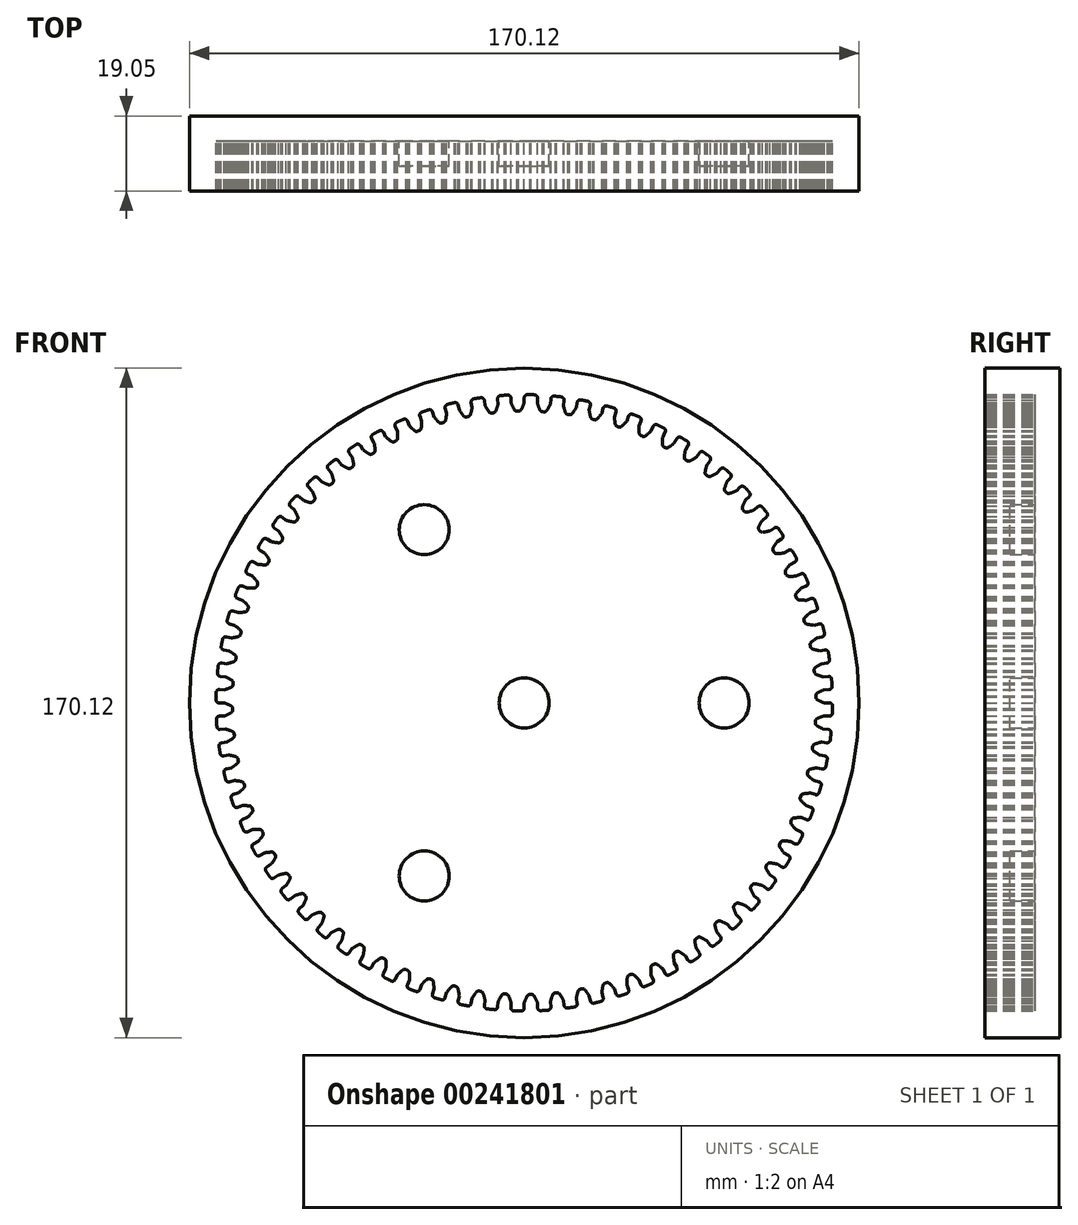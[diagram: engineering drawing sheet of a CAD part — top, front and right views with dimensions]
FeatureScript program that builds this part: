
annotation { "Feature Type Name" : "Feature", "Feature Type Description" : "" }
export const myFeature = defineFeature(function(context is Context, id is Id, definition is map)
    precondition{}
    {
        {
            var Q0;
            Q0=qCreatedBy(makeId("Front.planeOp"),FACE);
            var sketch = newSketch(context, id + "F0", { "sketchPlane" : qUnion([Q0])});
            skArc(sketch, "E0", {"start": v(-4.21, 78.2) * mm, "mid": v(-5.12, 78.15) * mm, "end": v(-6.03, 78.08) * mm});
            skLineSegment(sketch, "E1.MirrorCS", {"start": v(0, 76.2) * mm, "end": v(0, 77.53) * mm});
            skArc(sketch, "E2.MirrorCS", {"start": v(0, 76.2) * mm, "mid": v(-0.35, 75.36) * mm, "end": v(-0.73, 74.54) * mm});
            skArc(sketch, "E3.MirrorCS", {"start": v(-3.32, 76.13) * mm, "mid": v(-2.94, 75.3) * mm, "end": v(-2.52, 74.5) * mm});
            skLineSegment(sketch, "E4.MirrorCS", {"start": v(-3.32, 76.13) * mm, "end": v(-3.38, 77.45) * mm});
            skPoint(sketch, "E5.visualSharp", {"position": v(-2.27, 74.06) * mm});
            skArc(sketch, "E5.filletArc", {"start": v(-2.52, 74.5) * mm, "mid": v(-2.2, 74.19) * mm, "end": v(-1.78, 74.1) * mm});
            skPoint(sketch, "E6.visualSharp", {"position": v(-0.96, 74.09) * mm});
            skArc(sketch, "E6.filletArc", {"start": v(-1.45, 74.1) * mm, "mid": v(-1.03, 74.21) * mm, "end": v(-0.73, 74.54) * mm});
            skLineSegment(sketch, "E7", {"start": v(-1.78, 74.1) * mm, "end": v(-1.45, 74.1) * mm});
            skCircle(sketch, "E8", {"center": v(0, 0) * mm, "radius": 85.06 * mm});
            skPoint(sketch, "E9.visualSharp", {"position": v(-3.42, 78.24) * mm});
            skPoint(sketch, "E10.visualSharp", {"position": v(0, 78.32) * mm});
            skArc(sketch, "E11.filletArc", {"start": v(0.8, 78.31) * mm, "mid": v(0.23, 78.08) * mm, "end": v(0, 77.53) * mm});
            skArc(sketch, "E12.filletArc", {"start": v(-3.38, 77.45) * mm, "mid": v(-3.64, 78) * mm, "end": v(-4.21, 78.2) * mm});
            skArc(sketch, "E13.1.0", {"start": v(-10.12, 76.86) * mm, "mid": v(-10.42, 77.39) * mm, "end": v(-11.01, 77.54) * mm});
            skLineSegment(sketch, "E13.1.1", {"start": v(-9.95, 75.55) * mm, "end": v(-10.12, 76.86) * mm});
            skArc(sketch, "E13.1.2", {"start": v(-9.95, 75.55) * mm, "mid": v(-9.5, 74.76) * mm, "end": v(-9, 74) * mm});
            skArc(sketch, "E13.1.3", {"start": v(-9, 74) * mm, "mid": v(-8.66, 73.71) * mm, "end": v(-8.23, 73.66) * mm});
            skLineSegment(sketch, "E13.1.4", {"start": v(-8.23, 73.66) * mm, "end": v(-7.9, 73.7) * mm});
            skArc(sketch, "E13.1.5", {"start": v(-7.9, 73.7) * mm, "mid": v(-7.5, 73.84) * mm, "end": v(-7.23, 74.19) * mm});
            skArc(sketch, "E13.1.6", {"start": v(-6.64, 75.91) * mm, "mid": v(-6.91, 75.04) * mm, "end": v(-7.23, 74.19) * mm});
            skLineSegment(sketch, "E13.1.7", {"start": v(-6.64, 75.91) * mm, "end": v(-6.76, 77.23) * mm});
            skArc(sketch, "E13.1.8", {"start": v(-6.03, 78.08) * mm, "mid": v(-6.57, 77.8) * mm, "end": v(-6.76, 77.23) * mm});
            skArc(sketch, "E13.2.0", {"start": v(-16.78, 75.69) * mm, "mid": v(-17.13, 76.18) * mm, "end": v(-17.73, 76.28) * mm});
            skLineSegment(sketch, "E13.2.1", {"start": v(-16.5, 74.4) * mm, "end": v(-16.78, 75.69) * mm});
            skArc(sketch, "E13.2.2", {"start": v(-16.5, 74.4) * mm, "mid": v(-15.97, 73.65) * mm, "end": v(-15.42, 72.93) * mm});
            skArc(sketch, "E13.2.3", {"start": v(-15.42, 72.93) * mm, "mid": v(-15.06, 72.68) * mm, "end": v(-14.62, 72.66) * mm});
            skLineSegment(sketch, "E13.2.4", {"start": v(-14.62, 72.66) * mm, "end": v(-14.3, 72.72) * mm});
            skArc(sketch, "E13.2.5", {"start": v(-14.3, 72.72) * mm, "mid": v(-13.9, 72.9) * mm, "end": v(-13.66, 73.28) * mm});
            skArc(sketch, "E13.2.6", {"start": v(-13.23, 75.04) * mm, "mid": v(-13.43, 74.15) * mm, "end": v(-13.66, 73.28) * mm});
            skLineSegment(sketch, "E13.2.7", {"start": v(-13.23, 75.04) * mm, "end": v(-13.46, 76.35) * mm});
            skArc(sketch, "E13.2.8", {"start": v(-12.82, 77.26) * mm, "mid": v(-13.33, 76.94) * mm, "end": v(-13.46, 76.35) * mm});
            skArc(sketch, "E14.1.3.0", {"start": v(-23.31, 73.94) * mm, "mid": v(-23.7, 74.4) * mm, "end": v(-24.3, 74.45) * mm});
            skLineSegment(sketch, "E14.4.3.0", {"start": v(-22.91, 72.67) * mm, "end": v(-23.31, 73.94) * mm});
            skArc(sketch, "E14.7.3.0", {"start": v(-22.91, 72.67) * mm, "mid": v(-22.33, 71.98) * mm, "end": v(-21.71, 71.3) * mm});
            skArc(sketch, "E14.11.3.0", {"start": v(-21.71, 71.3) * mm, "mid": v(-21.33, 71.09) * mm, "end": v(-20.9, 71.1) * mm});
            skLineSegment(sketch, "E14.15.3.0", {"start": v(-20.9, 71.1) * mm, "end": v(-20.58, 71.2) * mm});
            skArc(sketch, "E14.18.3.0", {"start": v(-20.58, 71.2) * mm, "mid": v(-20.2, 71.42) * mm, "end": v(-20, 71.8) * mm});
            skArc(sketch, "E14.22.3.0", {"start": v(-19.72, 73.6) * mm, "mid": v(-19.84, 72.7) * mm, "end": v(-20, 71.8) * mm});
            skLineSegment(sketch, "E14.26.3.0", {"start": v(-19.72, 73.6) * mm, "end": v(-20.07, 74.88) * mm});
            skArc(sketch, "E14.29.3.0", {"start": v(-19.5, 75.85) * mm, "mid": v(-19.98, 75.48) * mm, "end": v(-20.07, 74.88) * mm});
            skArc(sketch, "E14.1.4.0", {"start": v(-29.67, 71.62) * mm, "mid": v(-30.1, 72.05) * mm, "end": v(-30.7, 72.05) * mm});
            skLineSegment(sketch, "E14.4.4.0", {"start": v(-29.16, 70.4) * mm, "end": v(-29.67, 71.62) * mm});
            skArc(sketch, "E14.7.4.0", {"start": v(-29.16, 70.4) * mm, "mid": v(-28.52, 69.76) * mm, "end": v(-27.85, 69.14) * mm});
            skArc(sketch, "E14.11.4.0", {"start": v(-27.85, 69.14) * mm, "mid": v(-27.45, 68.96) * mm, "end": v(-27.01, 69.02) * mm});
            skLineSegment(sketch, "E14.15.4.0", {"start": v(-27.01, 69.02) * mm, "end": v(-26.71, 69.13) * mm});
            skArc(sketch, "E14.18.4.0", {"start": v(-26.71, 69.13) * mm, "mid": v(-26.35, 69.39) * mm, "end": v(-26.18, 69.79) * mm});
            skArc(sketch, "E14.22.4.0", {"start": v(-26.06, 71.6) * mm, "mid": v(-26.1, 70.7) * mm, "end": v(-26.18, 69.79) * mm});
            skLineSegment(sketch, "E14.26.4.0", {"start": v(-26.06, 71.6) * mm, "end": v(-26.52, 72.85) * mm});
            skArc(sketch, "E14.29.4.0", {"start": v(-26.04, 73.86) * mm, "mid": v(-26.49, 73.46) * mm, "end": v(-26.52, 72.85) * mm});
            skArc(sketch, "E14.1.5.0", {"start": v(-35.8, 68.77) * mm, "mid": v(-36.26, 69.15) * mm, "end": v(-36.87, 69.1) * mm});
            skLineSegment(sketch, "E14.4.5.0", {"start": v(-35.19, 67.6) * mm, "end": v(-35.8, 68.77) * mm});
            skArc(sketch, "E14.7.5.0", {"start": v(-35.19, 67.6) * mm, "mid": v(-34.49, 67) * mm, "end": v(-33.77, 66.45) * mm});
            skArc(sketch, "E14.11.5.0", {"start": v(-33.77, 66.45) * mm, "mid": v(-33.35, 66.3) * mm, "end": v(-32.93, 66.4) * mm});
            skLineSegment(sketch, "E14.15.5.0", {"start": v(-32.93, 66.4) * mm, "end": v(-32.63, 66.54) * mm});
            skArc(sketch, "E14.18.5.0", {"start": v(-32.63, 66.54) * mm, "mid": v(-32.3, 66.82) * mm, "end": v(-32.16, 67.24) * mm});
            skArc(sketch, "E14.22.5.0", {"start": v(-32.2, 69.06) * mm, "mid": v(-32.16, 68.15) * mm, "end": v(-32.16, 67.24) * mm});
            skLineSegment(sketch, "E14.26.5.0", {"start": v(-32.2, 69.06) * mm, "end": v(-32.76, 70.26) * mm});
            skArc(sketch, "E14.29.5.0", {"start": v(-32.38, 71.31) * mm, "mid": v(-32.79, 70.87) * mm, "end": v(-32.76, 70.26) * mm});
            skArc(sketch, "E14.1.6.0", {"start": v(-41.65, 65.38) * mm, "mid": v(-42.15, 65.73) * mm, "end": v(-42.75, 65.62) * mm});
            skLineSegment(sketch, "E14.4.6.0", {"start": v(-40.94, 64.27) * mm, "end": v(-41.65, 65.38) * mm});
            skArc(sketch, "E14.7.6.0", {"start": v(-40.94, 64.27) * mm, "mid": v(-40.2, 63.74) * mm, "end": v(-39.43, 63.26) * mm});
            skArc(sketch, "E14.11.6.0", {"start": v(-39.43, 63.26) * mm, "mid": v(-39, 63.14) * mm, "end": v(-38.59, 63.28) * mm});
            skLineSegment(sketch, "E14.15.6.0", {"start": v(-38.59, 63.28) * mm, "end": v(-38.3, 63.45) * mm});
            skArc(sketch, "E14.18.6.0", {"start": v(-38.3, 63.45) * mm, "mid": v(-38, 63.76) * mm, "end": v(-37.9, 64.18) * mm});
            skArc(sketch, "E14.22.6.0", {"start": v(-38.1, 66) * mm, "mid": v(-37.98, 65.09) * mm, "end": v(-37.9, 64.18) * mm});
            skLineSegment(sketch, "E14.26.6.0", {"start": v(-38.1, 66) * mm, "end": v(-38.76, 67.14) * mm});
            skArc(sketch, "E14.29.6.0", {"start": v(-38.47, 68.22) * mm, "mid": v(-38.84, 67.74) * mm, "end": v(-38.76, 67.14) * mm});
            skArc(sketch, "E14.1.7.0", {"start": v(-47.2, 61.5) * mm, "mid": v(-47.72, 61.8) * mm, "end": v(-48.3, 61.65) * mm});
            skLineSegment(sketch, "E14.4.7.0", {"start": v(-46.39, 60.45) * mm, "end": v(-47.2, 61.5) * mm});
            skArc(sketch, "E14.7.7.0", {"start": v(-46.39, 60.45) * mm, "mid": v(-45.6, 60) * mm, "end": v(-44.8, 59.58) * mm});
            skArc(sketch, "E14.11.7.0", {"start": v(-44.8, 59.58) * mm, "mid": v(-44.36, 59.5) * mm, "end": v(-43.96, 59.67) * mm});
            skLineSegment(sketch, "E14.15.7.0", {"start": v(-43.96, 59.67) * mm, "end": v(-43.7, 59.86) * mm});
            skArc(sketch, "E14.18.7.0", {"start": v(-43.7, 59.86) * mm, "mid": v(-43.41, 60.2) * mm, "end": v(-43.35, 60.64) * mm});
            skArc(sketch, "E14.22.7.0", {"start": v(-43.7, 62.42) * mm, "mid": v(-43.5, 61.53) * mm, "end": v(-43.35, 60.64) * mm});
            skLineSegment(sketch, "E14.26.7.0", {"start": v(-43.7, 62.42) * mm, "end": v(-44.47, 63.5) * mm});
            skArc(sketch, "E14.29.7.0", {"start": v(-44.27, 64.6) * mm, "mid": v(-44.6, 64.1) * mm, "end": v(-44.47, 63.5) * mm});
            skArc(sketch, "E14.1.8.0", {"start": v(-52.38, 57.16) * mm, "mid": v(-52.93, 57.41) * mm, "end": v(-53.5, 57.2) * mm});
            skLineSegment(sketch, "E14.4.8.0", {"start": v(-51.48, 56.18) * mm, "end": v(-52.38, 57.16) * mm});
            skArc(sketch, "E14.7.8.0", {"start": v(-51.48, 56.18) * mm, "mid": v(-50.66, 55.8) * mm, "end": v(-49.82, 55.45) * mm});
            skArc(sketch, "E14.11.8.0", {"start": v(-49.82, 55.45) * mm, "mid": v(-49.38, 55.41) * mm, "end": v(-48.99, 55.62) * mm});
            skLineSegment(sketch, "E14.15.8.0", {"start": v(-48.99, 55.62) * mm, "end": v(-48.75, 55.83) * mm});
            skArc(sketch, "E14.18.8.0", {"start": v(-48.75, 55.83) * mm, "mid": v(-48.5, 56.19) * mm, "end": v(-48.47, 56.63) * mm});
            skArc(sketch, "E14.22.8.0", {"start": v(-48.98, 58.37) * mm, "mid": v(-48.7, 57.5) * mm, "end": v(-48.47, 56.63) * mm});
            skLineSegment(sketch, "E14.26.8.0", {"start": v(-48.98, 58.37) * mm, "end": v(-49.83, 59.39) * mm});
            skArc(sketch, "E14.29.8.0", {"start": v(-49.73, 60.5) * mm, "mid": v(-50.01, 59.97) * mm, "end": v(-49.83, 59.39) * mm});
            skArc(sketch, "E14.1.9.0", {"start": v(-57.16, 52.38) * mm, "mid": v(-57.73, 52.58) * mm, "end": v(-58.28, 52.32) * mm});
            skLineSegment(sketch, "E14.4.9.0", {"start": v(-56.18, 51.48) * mm, "end": v(-57.16, 52.38) * mm});
            skArc(sketch, "E14.7.9.0", {"start": v(-56.18, 51.48) * mm, "mid": v(-55.33, 51.17) * mm, "end": v(-54.46, 50.9) * mm});
            skArc(sketch, "E14.11.9.0", {"start": v(-54.46, 50.9) * mm, "mid": v(-54.02, 50.9) * mm, "end": v(-53.65, 51.13) * mm});
            skLineSegment(sketch, "E14.15.9.0", {"start": v(-53.65, 51.13) * mm, "end": v(-53.43, 51.37) * mm});
            skArc(sketch, "E14.18.9.0", {"start": v(-53.43, 51.37) * mm, "mid": v(-53.2, 51.75) * mm, "end": v(-53.22, 52.19) * mm});
            skArc(sketch, "E14.22.9.0", {"start": v(-53.88, 53.88) * mm, "mid": v(-53.53, 53.04) * mm, "end": v(-53.22, 52.19) * mm});
            skLineSegment(sketch, "E14.26.9.0", {"start": v(-53.88, 53.88) * mm, "end": v(-54.82, 54.82) * mm});
            skArc(sketch, "E14.29.9.0", {"start": v(-54.81, 55.94) * mm, "mid": v(-55.05, 55.38) * mm, "end": v(-54.82, 54.82) * mm});
            skArc(sketch, "E14.1.10.0", {"start": v(-61.5, 47.2) * mm, "mid": v(-62.1, 47.35) * mm, "end": v(-62.61, 47.04) * mm});
            skLineSegment(sketch, "E14.4.10.0", {"start": v(-60.45, 46.39) * mm, "end": v(-61.5, 47.2) * mm});
            skArc(sketch, "E14.7.10.0", {"start": v(-60.45, 46.39) * mm, "mid": v(-59.58, 46.15) * mm, "end": v(-58.69, 45.96) * mm});
            skArc(sketch, "E14.11.10.0", {"start": v(-58.69, 45.96) * mm, "mid": v(-58.25, 46) * mm, "end": v(-57.9, 46.26) * mm});
            skLineSegment(sketch, "E14.15.10.0", {"start": v(-57.9, 46.26) * mm, "end": v(-57.7, 46.52) * mm});
            skArc(sketch, "E14.18.10.0", {"start": v(-57.7, 46.52) * mm, "mid": v(-57.51, 46.91) * mm, "end": v(-57.57, 47.35) * mm});
            skArc(sketch, "E14.22.10.0", {"start": v(-58.37, 48.98) * mm, "mid": v(-57.95, 48.17) * mm, "end": v(-57.57, 47.35) * mm});
            skLineSegment(sketch, "E14.26.10.0", {"start": v(-58.37, 48.98) * mm, "end": v(-59.39, 49.83) * mm});
            skArc(sketch, "E14.29.10.0", {"start": v(-59.48, 50.95) * mm, "mid": v(-59.67, 50.37) * mm, "end": v(-59.39, 49.83) * mm});
            skArc(sketch, "E14.1.11.0", {"start": v(-65.38, 41.65) * mm, "mid": v(-65.98, 41.76) * mm, "end": v(-66.48, 41.4) * mm});
            skLineSegment(sketch, "E14.4.11.0", {"start": v(-64.27, 40.94) * mm, "end": v(-65.38, 41.65) * mm});
            skArc(sketch, "E14.7.11.0", {"start": v(-64.27, 40.94) * mm, "mid": v(-63.37, 40.78) * mm, "end": v(-62.47, 40.67) * mm});
            skArc(sketch, "E14.11.11.0", {"start": v(-62.47, 40.67) * mm, "mid": v(-62.04, 40.74) * mm, "end": v(-61.71, 41.04) * mm});
            skLineSegment(sketch, "E14.15.11.0", {"start": v(-61.71, 41.04) * mm, "end": v(-61.53, 41.31) * mm});
            skArc(sketch, "E14.18.11.0", {"start": v(-61.53, 41.31) * mm, "mid": v(-61.38, 41.72) * mm, "end": v(-61.48, 42.15) * mm});
            skArc(sketch, "E14.22.11.0", {"start": v(-62.42, 43.7) * mm, "mid": v(-61.93, 42.94) * mm, "end": v(-61.48, 42.15) * mm});
            skLineSegment(sketch, "E14.26.11.0", {"start": v(-62.42, 43.7) * mm, "end": v(-63.5, 44.47) * mm});
            skArc(sketch, "E14.29.11.0", {"start": v(-63.7, 45.57) * mm, "mid": v(-63.83, 44.98) * mm, "end": v(-63.5, 44.47) * mm});
            skArc(sketch, "E14.1.12.0", {"start": v(-68.77, 35.8) * mm, "mid": v(-69.37, 35.85) * mm, "end": v(-69.83, 35.46) * mm});
            skLineSegment(sketch, "E14.4.12.0", {"start": v(-67.6, 35.19) * mm, "end": v(-68.77, 35.8) * mm});
            skArc(sketch, "E14.7.12.0", {"start": v(-67.6, 35.19) * mm, "mid": v(-66.68, 35.1) * mm, "end": v(-65.78, 35.07) * mm});
            skArc(sketch, "E14.11.12.0", {"start": v(-65.78, 35.07) * mm, "mid": v(-65.35, 35.18) * mm, "end": v(-65.06, 35.5) * mm});
            skLineSegment(sketch, "E14.15.12.0", {"start": v(-65.06, 35.5) * mm, "end": v(-64.9, 35.8) * mm});
            skArc(sketch, "E14.18.12.0", {"start": v(-64.9, 35.8) * mm, "mid": v(-64.79, 36.21) * mm, "end": v(-64.92, 36.63) * mm});
            skArc(sketch, "E14.22.12.0", {"start": v(-66, 38.1) * mm, "mid": v(-65.44, 37.38) * mm, "end": v(-64.92, 36.63) * mm});
            skLineSegment(sketch, "E14.26.12.0", {"start": v(-66, 38.1) * mm, "end": v(-67.14, 38.76) * mm});
            skArc(sketch, "E14.29.12.0", {"start": v(-67.42, 39.85) * mm, "mid": v(-67.5, 39.24) * mm, "end": v(-67.14, 38.76) * mm});
            skArc(sketch, "E14.1.13.0", {"start": v(-71.62, 29.67) * mm, "mid": v(-72.23, 29.67) * mm, "end": v(-72.66, 29.23) * mm});
            skLineSegment(sketch, "E14.4.13.0", {"start": v(-70.4, 29.16) * mm, "end": v(-71.62, 29.67) * mm});
            skArc(sketch, "E14.7.13.0", {"start": v(-70.4, 29.16) * mm, "mid": v(-69.5, 29.16) * mm, "end": v(-68.58, 29.2) * mm});
            skArc(sketch, "E14.11.13.0", {"start": v(-68.58, 29.2) * mm, "mid": v(-68.17, 29.35) * mm, "end": v(-67.9, 29.7) * mm});
            skLineSegment(sketch, "E14.15.13.0", {"start": v(-67.9, 29.7) * mm, "end": v(-67.77, 30) * mm});
            skArc(sketch, "E14.18.13.0", {"start": v(-67.77, 30) * mm, "mid": v(-67.7, 30.43) * mm, "end": v(-67.86, 30.84) * mm});
            skArc(sketch, "E14.22.13.0", {"start": v(-69.06, 32.2) * mm, "mid": v(-68.45, 31.53) * mm, "end": v(-67.86, 30.84) * mm});
            skLineSegment(sketch, "E14.26.13.0", {"start": v(-69.06, 32.2) * mm, "end": v(-70.26, 32.76) * mm});
            skArc(sketch, "E14.29.13.0", {"start": v(-70.64, 33.82) * mm, "mid": v(-70.67, 33.21) * mm, "end": v(-70.26, 32.76) * mm});
            skArc(sketch, "E14.1.14.0", {"start": v(-73.94, 23.31) * mm, "mid": v(-74.54, 23.26) * mm, "end": v(-74.93, 22.8) * mm});
            skLineSegment(sketch, "E14.4.14.0", {"start": v(-72.67, 22.91) * mm, "end": v(-73.94, 23.31) * mm});
            skArc(sketch, "E14.7.14.0", {"start": v(-72.67, 22.91) * mm, "mid": v(-71.77, 23) * mm, "end": v(-70.87, 23.11) * mm});
            skArc(sketch, "E14.11.14.0", {"start": v(-70.87, 23.11) * mm, "mid": v(-70.47, 23.3) * mm, "end": v(-70.23, 23.67) * mm});
            skLineSegment(sketch, "E14.15.14.0", {"start": v(-70.23, 23.67) * mm, "end": v(-70.13, 23.98) * mm});
            skArc(sketch, "E14.18.14.0", {"start": v(-70.13, 23.98) * mm, "mid": v(-70.1, 24.41) * mm, "end": v(-70.3, 24.8) * mm});
            skArc(sketch, "E14.22.14.0", {"start": v(-71.6, 26.06) * mm, "mid": v(-70.93, 25.45) * mm, "end": v(-70.3, 24.8) * mm});
            skLineSegment(sketch, "E14.26.14.0", {"start": v(-71.6, 26.06) * mm, "end": v(-72.85, 26.52) * mm});
            skArc(sketch, "E14.29.14.0", {"start": v(-73.32, 27.53) * mm, "mid": v(-73.3, 26.93) * mm, "end": v(-72.85, 26.52) * mm});
            skArc(sketch, "E14.1.15.0", {"start": v(-75.69, 16.78) * mm, "mid": v(-76.28, 16.67) * mm, "end": v(-76.63, 16.17) * mm});
            skLineSegment(sketch, "E14.4.15.0", {"start": v(-74.4, 16.5) * mm, "end": v(-75.69, 16.78) * mm});
            skArc(sketch, "E14.7.15.0", {"start": v(-74.4, 16.5) * mm, "mid": v(-73.5, 16.65) * mm, "end": v(-72.61, 16.85) * mm});
            skArc(sketch, "E14.11.15.0", {"start": v(-72.61, 16.85) * mm, "mid": v(-72.23, 17.07) * mm, "end": v(-72.03, 17.46) * mm});
            skLineSegment(sketch, "E14.15.15.0", {"start": v(-72.03, 17.46) * mm, "end": v(-71.95, 17.77) * mm});
            skArc(sketch, "E14.18.15.0", {"start": v(-71.95, 17.77) * mm, "mid": v(-71.95, 18.21) * mm, "end": v(-72.19, 18.58) * mm});
            skArc(sketch, "E14.22.15.0", {"start": v(-73.6, 19.72) * mm, "mid": v(-72.88, 19.17) * mm, "end": v(-72.19, 18.58) * mm});
            skLineSegment(sketch, "E14.26.15.0", {"start": v(-73.6, 19.72) * mm, "end": v(-74.88, 20.07) * mm});
            skArc(sketch, "E14.29.15.0", {"start": v(-75.44, 21.04) * mm, "mid": v(-75.36, 20.44) * mm, "end": v(-74.88, 20.07) * mm});
            skArc(sketch, "E14.1.16.0", {"start": v(-76.86, 10.12) * mm, "mid": v(-77.45, 9.96) * mm, "end": v(-77.75, 9.43) * mm});
            skLineSegment(sketch, "E14.4.16.0", {"start": v(-75.55, 9.95) * mm, "end": v(-76.86, 10.12) * mm});
            skArc(sketch, "E14.7.16.0", {"start": v(-75.55, 9.95) * mm, "mid": v(-74.67, 10.18) * mm, "end": v(-73.8, 10.46) * mm});
            skArc(sketch, "E14.11.16.0", {"start": v(-73.8, 10.46) * mm, "mid": v(-73.44, 10.7) * mm, "end": v(-73.28, 11.11) * mm});
            skLineSegment(sketch, "E14.15.16.0", {"start": v(-73.28, 11.11) * mm, "end": v(-73.23, 11.43) * mm});
            skArc(sketch, "E14.18.16.0", {"start": v(-73.23, 11.43) * mm, "mid": v(-73.26, 11.87) * mm, "end": v(-73.53, 12.22) * mm});
            skArc(sketch, "E14.22.16.0", {"start": v(-75.04, 13.23) * mm, "mid": v(-74.27, 12.74) * mm, "end": v(-73.53, 12.22) * mm});
            skLineSegment(sketch, "E14.26.16.0", {"start": v(-75.04, 13.23) * mm, "end": v(-76.35, 13.46) * mm});
            skArc(sketch, "E14.29.16.0", {"start": v(-76.98, 14.38) * mm, "mid": v(-76.86, 13.79) * mm, "end": v(-76.35, 13.46) * mm});
            skArc(sketch, "E14.1.17.0", {"start": v(-77.45, 3.38) * mm, "mid": v(-78.02, 3.17) * mm, "end": v(-78.27, 2.62) * mm});
            skLineSegment(sketch, "E14.4.17.0", {"start": v(-76.13, 3.32) * mm, "end": v(-77.45, 3.38) * mm});
            skArc(sketch, "E14.7.17.0", {"start": v(-76.13, 3.32) * mm, "mid": v(-75.27, 3.63) * mm, "end": v(-74.43, 3.98) * mm});
            skArc(sketch, "E14.11.17.0", {"start": v(-74.43, 3.98) * mm, "mid": v(-74.1, 4.27) * mm, "end": v(-73.97, 4.69) * mm});
            skLineSegment(sketch, "E14.15.17.0", {"start": v(-73.97, 4.69) * mm, "end": v(-73.94, 5) * mm});
            skArc(sketch, "E14.18.17.0", {"start": v(-73.94, 5) * mm, "mid": v(-74.02, 5.44) * mm, "end": v(-74.32, 5.77) * mm});
            skArc(sketch, "E14.22.17.0", {"start": v(-75.91, 6.64) * mm, "mid": v(-75.1, 6.22) * mm, "end": v(-74.32, 5.77) * mm});
            skLineSegment(sketch, "E14.26.17.0", {"start": v(-75.91, 6.64) * mm, "end": v(-77.23, 6.76) * mm});
            skArc(sketch, "E14.29.17.0", {"start": v(-77.95, 7.62) * mm, "mid": v(-77.77, 7.04) * mm, "end": v(-77.23, 6.76) * mm});
            skArc(sketch, "E14.1.18.0", {"start": v(-77.45, -3.38) * mm, "mid": v(-78, -3.64) * mm, "end": v(-78.2, -4.21) * mm});
            skLineSegment(sketch, "E14.4.18.0", {"start": v(-76.13, -3.32) * mm, "end": v(-77.45, -3.38) * mm});
            skArc(sketch, "E14.7.18.0", {"start": v(-76.13, -3.32) * mm, "mid": v(-75.3, -2.94) * mm, "end": v(-74.5, -2.52) * mm});
            skArc(sketch, "E14.11.18.0", {"start": v(-74.5, -2.52) * mm, "mid": v(-74.19, -2.2) * mm, "end": v(-74.1, -1.78) * mm});
            skLineSegment(sketch, "E14.15.18.0", {"start": v(-74.1, -1.78) * mm, "end": v(-74.1, -1.45) * mm});
            skArc(sketch, "E14.18.18.0", {"start": v(-74.1, -1.45) * mm, "mid": v(-74.21, -1.03) * mm, "end": v(-74.54, -0.73) * mm});
            skArc(sketch, "E14.22.18.0", {"start": v(-76.2, 0) * mm, "mid": v(-75.36, -0.35) * mm, "end": v(-74.54, -0.73) * mm});
            skLineSegment(sketch, "E14.26.18.0", {"start": v(-76.2, 0) * mm, "end": v(-77.53, 0) * mm});
            skArc(sketch, "E14.29.18.0", {"start": v(-78.31, 0.8) * mm, "mid": v(-78.08, 0.23) * mm, "end": v(-77.53, 0) * mm});
            skArc(sketch, "E14.1.19.0", {"start": v(-76.86, -10.12) * mm, "mid": v(-77.39, -10.42) * mm, "end": v(-77.54, -11.01) * mm});
            skLineSegment(sketch, "E14.4.19.0", {"start": v(-75.55, -9.95) * mm, "end": v(-76.86, -10.12) * mm});
            skArc(sketch, "E14.7.19.0", {"start": v(-75.55, -9.95) * mm, "mid": v(-74.76, -9.5) * mm, "end": v(-74, -9) * mm});
            skArc(sketch, "E14.11.19.0", {"start": v(-74, -9) * mm, "mid": v(-73.71, -8.66) * mm, "end": v(-73.66, -8.23) * mm});
            skLineSegment(sketch, "E14.15.19.0", {"start": v(-73.66, -8.23) * mm, "end": v(-73.7, -7.9) * mm});
            skArc(sketch, "E14.18.19.0", {"start": v(-73.7, -7.9) * mm, "mid": v(-73.84, -7.5) * mm, "end": v(-74.19, -7.23) * mm});
            skArc(sketch, "E14.22.19.0", {"start": v(-75.91, -6.64) * mm, "mid": v(-75.04, -6.91) * mm, "end": v(-74.19, -7.23) * mm});
            skLineSegment(sketch, "E14.26.19.0", {"start": v(-75.91, -6.64) * mm, "end": v(-77.23, -6.76) * mm});
            skArc(sketch, "E14.29.19.0", {"start": v(-78.08, -6.03) * mm, "mid": v(-77.8, -6.57) * mm, "end": v(-77.23, -6.76) * mm});
            skArc(sketch, "E14.1.20.0", {"start": v(-75.69, -16.78) * mm, "mid": v(-76.18, -17.13) * mm, "end": v(-76.28, -17.73) * mm});
            skLineSegment(sketch, "E14.4.20.0", {"start": v(-74.4, -16.5) * mm, "end": v(-75.69, -16.78) * mm});
            skArc(sketch, "E14.7.20.0", {"start": v(-74.4, -16.5) * mm, "mid": v(-73.65, -15.97) * mm, "end": v(-72.93, -15.42) * mm});
            skArc(sketch, "E14.11.20.0", {"start": v(-72.93, -15.42) * mm, "mid": v(-72.68, -15.06) * mm, "end": v(-72.66, -14.62) * mm});
            skLineSegment(sketch, "E14.15.20.0", {"start": v(-72.66, -14.62) * mm, "end": v(-72.72, -14.3) * mm});
            skArc(sketch, "E14.18.20.0", {"start": v(-72.72, -14.3) * mm, "mid": v(-72.9, -13.9) * mm, "end": v(-73.28, -13.66) * mm});
            skArc(sketch, "E14.22.20.0", {"start": v(-75.04, -13.23) * mm, "mid": v(-74.15, -13.43) * mm, "end": v(-73.28, -13.66) * mm});
            skLineSegment(sketch, "E14.26.20.0", {"start": v(-75.04, -13.23) * mm, "end": v(-76.35, -13.46) * mm});
            skArc(sketch, "E14.29.20.0", {"start": v(-77.26, -12.82) * mm, "mid": v(-76.94, -13.33) * mm, "end": v(-76.35, -13.46) * mm});
            skArc(sketch, "E14.1.21.0", {"start": v(-73.94, -23.31) * mm, "mid": v(-74.4, -23.7) * mm, "end": v(-74.45, -24.3) * mm});
            skLineSegment(sketch, "E14.4.21.0", {"start": v(-72.67, -22.91) * mm, "end": v(-73.94, -23.31) * mm});
            skArc(sketch, "E14.7.21.0", {"start": v(-72.67, -22.91) * mm, "mid": v(-71.98, -22.33) * mm, "end": v(-71.3, -21.71) * mm});
            skArc(sketch, "E14.11.21.0", {"start": v(-71.3, -21.71) * mm, "mid": v(-71.09, -21.33) * mm, "end": v(-71.1, -20.9) * mm});
            skLineSegment(sketch, "E14.15.21.0", {"start": v(-71.1, -20.9) * mm, "end": v(-71.2, -20.58) * mm});
            skArc(sketch, "E14.18.21.0", {"start": v(-71.2, -20.58) * mm, "mid": v(-71.42, -20.2) * mm, "end": v(-71.8, -20) * mm});
            skArc(sketch, "E14.22.21.0", {"start": v(-73.6, -19.72) * mm, "mid": v(-72.7, -19.84) * mm, "end": v(-71.8, -20) * mm});
            skLineSegment(sketch, "E14.26.21.0", {"start": v(-73.6, -19.72) * mm, "end": v(-74.88, -20.07) * mm});
            skArc(sketch, "E14.29.21.0", {"start": v(-75.85, -19.5) * mm, "mid": v(-75.48, -19.98) * mm, "end": v(-74.88, -20.07) * mm});
            skArc(sketch, "E14.1.22.0", {"start": v(-71.62, -29.67) * mm, "mid": v(-72.05, -30.1) * mm, "end": v(-72.05, -30.7) * mm});
            skLineSegment(sketch, "E14.4.22.0", {"start": v(-70.4, -29.16) * mm, "end": v(-71.62, -29.67) * mm});
            skArc(sketch, "E14.7.22.0", {"start": v(-70.4, -29.16) * mm, "mid": v(-69.76, -28.52) * mm, "end": v(-69.14, -27.85) * mm});
            skArc(sketch, "E14.11.22.0", {"start": v(-69.14, -27.85) * mm, "mid": v(-68.96, -27.45) * mm, "end": v(-69.02, -27.01) * mm});
            skLineSegment(sketch, "E14.15.22.0", {"start": v(-69.02, -27.01) * mm, "end": v(-69.13, -26.71) * mm});
            skArc(sketch, "E14.18.22.0", {"start": v(-69.13, -26.71) * mm, "mid": v(-69.39, -26.35) * mm, "end": v(-69.79, -26.18) * mm});
            skArc(sketch, "E14.22.22.0", {"start": v(-71.6, -26.06) * mm, "mid": v(-70.7, -26.1) * mm, "end": v(-69.79, -26.18) * mm});
            skLineSegment(sketch, "E14.26.22.0", {"start": v(-71.6, -26.06) * mm, "end": v(-72.85, -26.52) * mm});
            skArc(sketch, "E14.29.22.0", {"start": v(-73.86, -26.04) * mm, "mid": v(-73.46, -26.49) * mm, "end": v(-72.85, -26.52) * mm});
            skArc(sketch, "E14.1.23.0", {"start": v(-68.77, -35.8) * mm, "mid": v(-69.15, -36.26) * mm, "end": v(-69.1, -36.87) * mm});
            skLineSegment(sketch, "E14.4.23.0", {"start": v(-67.6, -35.19) * mm, "end": v(-68.77, -35.8) * mm});
            skArc(sketch, "E14.7.23.0", {"start": v(-67.6, -35.19) * mm, "mid": v(-67, -34.49) * mm, "end": v(-66.45, -33.77) * mm});
            skArc(sketch, "E14.11.23.0", {"start": v(-66.45, -33.77) * mm, "mid": v(-66.3, -33.35) * mm, "end": v(-66.4, -32.93) * mm});
            skLineSegment(sketch, "E14.15.23.0", {"start": v(-66.4, -32.93) * mm, "end": v(-66.54, -32.63) * mm});
            skArc(sketch, "E14.18.23.0", {"start": v(-66.54, -32.63) * mm, "mid": v(-66.82, -32.3) * mm, "end": v(-67.24, -32.16) * mm});
            skArc(sketch, "E14.22.23.0", {"start": v(-69.06, -32.2) * mm, "mid": v(-68.15, -32.16) * mm, "end": v(-67.24, -32.16) * mm});
            skLineSegment(sketch, "E14.26.23.0", {"start": v(-69.06, -32.2) * mm, "end": v(-70.26, -32.76) * mm});
            skArc(sketch, "E14.29.23.0", {"start": v(-71.31, -32.38) * mm, "mid": v(-70.87, -32.79) * mm, "end": v(-70.26, -32.76) * mm});
            skArc(sketch, "E14.1.24.0", {"start": v(-65.38, -41.65) * mm, "mid": v(-65.73, -42.15) * mm, "end": v(-65.62, -42.75) * mm});
            skLineSegment(sketch, "E14.4.24.0", {"start": v(-64.27, -40.94) * mm, "end": v(-65.38, -41.65) * mm});
            skArc(sketch, "E14.7.24.0", {"start": v(-64.27, -40.94) * mm, "mid": v(-63.74, -40.2) * mm, "end": v(-63.26, -39.43) * mm});
            skArc(sketch, "E14.11.24.0", {"start": v(-63.26, -39.43) * mm, "mid": v(-63.14, -39) * mm, "end": v(-63.28, -38.59) * mm});
            skLineSegment(sketch, "E14.15.24.0", {"start": v(-63.28, -38.59) * mm, "end": v(-63.45, -38.3) * mm});
            skArc(sketch, "E14.18.24.0", {"start": v(-63.45, -38.3) * mm, "mid": v(-63.76, -38) * mm, "end": v(-64.18, -37.9) * mm});
            skArc(sketch, "E14.22.24.0", {"start": v(-66, -38.1) * mm, "mid": v(-65.09, -37.98) * mm, "end": v(-64.18, -37.9) * mm});
            skLineSegment(sketch, "E14.26.24.0", {"start": v(-66, -38.1) * mm, "end": v(-67.14, -38.76) * mm});
            skArc(sketch, "E14.29.24.0", {"start": v(-68.22, -38.47) * mm, "mid": v(-67.74, -38.84) * mm, "end": v(-67.14, -38.76) * mm});
            skArc(sketch, "E14.1.25.0", {"start": v(-61.5, -47.2) * mm, "mid": v(-61.8, -47.72) * mm, "end": v(-61.65, -48.3) * mm});
            skLineSegment(sketch, "E14.4.25.0", {"start": v(-60.45, -46.39) * mm, "end": v(-61.5, -47.2) * mm});
            skArc(sketch, "E14.7.25.0", {"start": v(-60.45, -46.39) * mm, "mid": v(-60, -45.6) * mm, "end": v(-59.58, -44.8) * mm});
            skArc(sketch, "E14.11.25.0", {"start": v(-59.58, -44.8) * mm, "mid": v(-59.5, -44.36) * mm, "end": v(-59.67, -43.96) * mm});
            skLineSegment(sketch, "E14.15.25.0", {"start": v(-59.67, -43.96) * mm, "end": v(-59.86, -43.7) * mm});
            skArc(sketch, "E14.18.25.0", {"start": v(-59.86, -43.7) * mm, "mid": v(-60.2, -43.41) * mm, "end": v(-60.64, -43.35) * mm});
            skArc(sketch, "E14.22.25.0", {"start": v(-62.42, -43.7) * mm, "mid": v(-61.53, -43.5) * mm, "end": v(-60.64, -43.35) * mm});
            skLineSegment(sketch, "E14.26.25.0", {"start": v(-62.42, -43.7) * mm, "end": v(-63.5, -44.47) * mm});
            skArc(sketch, "E14.29.25.0", {"start": v(-64.6, -44.27) * mm, "mid": v(-64.1, -44.6) * mm, "end": v(-63.5, -44.47) * mm});
            skArc(sketch, "E14.1.26.0", {"start": v(-57.16, -52.38) * mm, "mid": v(-57.41, -52.93) * mm, "end": v(-57.2, -53.5) * mm});
            skLineSegment(sketch, "E14.4.26.0", {"start": v(-56.18, -51.48) * mm, "end": v(-57.16, -52.38) * mm});
            skArc(sketch, "E14.7.26.0", {"start": v(-56.18, -51.48) * mm, "mid": v(-55.8, -50.66) * mm, "end": v(-55.45, -49.82) * mm});
            skArc(sketch, "E14.11.26.0", {"start": v(-55.45, -49.82) * mm, "mid": v(-55.41, -49.38) * mm, "end": v(-55.62, -48.99) * mm});
            skLineSegment(sketch, "E14.15.26.0", {"start": v(-55.62, -48.99) * mm, "end": v(-55.83, -48.75) * mm});
            skArc(sketch, "E14.18.26.0", {"start": v(-55.83, -48.75) * mm, "mid": v(-56.19, -48.5) * mm, "end": v(-56.63, -48.47) * mm});
            skArc(sketch, "E14.22.26.0", {"start": v(-58.37, -48.98) * mm, "mid": v(-57.5, -48.7) * mm, "end": v(-56.63, -48.47) * mm});
            skLineSegment(sketch, "E14.26.26.0", {"start": v(-58.37, -48.98) * mm, "end": v(-59.39, -49.83) * mm});
            skArc(sketch, "E14.29.26.0", {"start": v(-60.5, -49.73) * mm, "mid": v(-59.97, -50.01) * mm, "end": v(-59.39, -49.83) * mm});
            skArc(sketch, "E14.1.27.0", {"start": v(-52.38, -57.16) * mm, "mid": v(-52.58, -57.73) * mm, "end": v(-52.32, -58.28) * mm});
            skLineSegment(sketch, "E14.4.27.0", {"start": v(-51.48, -56.18) * mm, "end": v(-52.38, -57.16) * mm});
            skArc(sketch, "E14.7.27.0", {"start": v(-51.48, -56.18) * mm, "mid": v(-51.17, -55.33) * mm, "end": v(-50.9, -54.46) * mm});
            skArc(sketch, "E14.11.27.0", {"start": v(-50.9, -54.46) * mm, "mid": v(-50.9, -54.02) * mm, "end": v(-51.13, -53.65) * mm});
            skLineSegment(sketch, "E14.15.27.0", {"start": v(-51.13, -53.65) * mm, "end": v(-51.37, -53.43) * mm});
            skArc(sketch, "E14.18.27.0", {"start": v(-51.37, -53.43) * mm, "mid": v(-51.75, -53.2) * mm, "end": v(-52.19, -53.22) * mm});
            skArc(sketch, "E14.22.27.0", {"start": v(-53.88, -53.88) * mm, "mid": v(-53.04, -53.53) * mm, "end": v(-52.19, -53.22) * mm});
            skLineSegment(sketch, "E14.26.27.0", {"start": v(-53.88, -53.88) * mm, "end": v(-54.82, -54.82) * mm});
            skArc(sketch, "E14.29.27.0", {"start": v(-55.94, -54.81) * mm, "mid": v(-55.38, -55.05) * mm, "end": v(-54.82, -54.82) * mm});
            skArc(sketch, "E14.1.28.0", {"start": v(-47.2, -61.5) * mm, "mid": v(-47.35, -62.1) * mm, "end": v(-47.04, -62.61) * mm});
            skLineSegment(sketch, "E14.4.28.0", {"start": v(-46.39, -60.45) * mm, "end": v(-47.2, -61.5) * mm});
            skArc(sketch, "E14.7.28.0", {"start": v(-46.39, -60.45) * mm, "mid": v(-46.15, -59.58) * mm, "end": v(-45.96, -58.69) * mm});
            skArc(sketch, "E14.11.28.0", {"start": v(-45.96, -58.69) * mm, "mid": v(-46, -58.25) * mm, "end": v(-46.26, -57.9) * mm});
            skLineSegment(sketch, "E14.15.28.0", {"start": v(-46.26, -57.9) * mm, "end": v(-46.52, -57.7) * mm});
            skArc(sketch, "E14.18.28.0", {"start": v(-46.52, -57.7) * mm, "mid": v(-46.91, -57.51) * mm, "end": v(-47.35, -57.57) * mm});
            skArc(sketch, "E14.22.28.0", {"start": v(-48.98, -58.37) * mm, "mid": v(-48.17, -57.95) * mm, "end": v(-47.35, -57.57) * mm});
            skLineSegment(sketch, "E14.26.28.0", {"start": v(-48.98, -58.37) * mm, "end": v(-49.83, -59.39) * mm});
            skArc(sketch, "E14.29.28.0", {"start": v(-50.95, -59.48) * mm, "mid": v(-50.37, -59.67) * mm, "end": v(-49.83, -59.39) * mm});
            skArc(sketch, "E14.1.29.0", {"start": v(-41.65, -65.38) * mm, "mid": v(-41.76, -65.98) * mm, "end": v(-41.4, -66.48) * mm});
            skLineSegment(sketch, "E14.4.29.0", {"start": v(-40.94, -64.27) * mm, "end": v(-41.65, -65.38) * mm});
            skArc(sketch, "E14.7.29.0", {"start": v(-40.94, -64.27) * mm, "mid": v(-40.78, -63.37) * mm, "end": v(-40.67, -62.47) * mm});
            skArc(sketch, "E14.11.29.0", {"start": v(-40.67, -62.47) * mm, "mid": v(-40.74, -62.04) * mm, "end": v(-41.04, -61.71) * mm});
            skLineSegment(sketch, "E14.15.29.0", {"start": v(-41.04, -61.71) * mm, "end": v(-41.31, -61.53) * mm});
            skArc(sketch, "E14.18.29.0", {"start": v(-41.31, -61.53) * mm, "mid": v(-41.72, -61.38) * mm, "end": v(-42.15, -61.48) * mm});
            skArc(sketch, "E14.22.29.0", {"start": v(-43.7, -62.42) * mm, "mid": v(-42.94, -61.93) * mm, "end": v(-42.15, -61.48) * mm});
            skLineSegment(sketch, "E14.26.29.0", {"start": v(-43.7, -62.42) * mm, "end": v(-44.47, -63.5) * mm});
            skArc(sketch, "E14.29.29.0", {"start": v(-45.57, -63.7) * mm, "mid": v(-44.98, -63.83) * mm, "end": v(-44.47, -63.5) * mm});
            skArc(sketch, "E14.1.30.0", {"start": v(-35.8, -68.77) * mm, "mid": v(-35.85, -69.37) * mm, "end": v(-35.46, -69.83) * mm});
            skLineSegment(sketch, "E14.4.30.0", {"start": v(-35.19, -67.6) * mm, "end": v(-35.8, -68.77) * mm});
            skArc(sketch, "E14.7.30.0", {"start": v(-35.19, -67.6) * mm, "mid": v(-35.1, -66.68) * mm, "end": v(-35.07, -65.78) * mm});
            skArc(sketch, "E14.11.30.0", {"start": v(-35.07, -65.78) * mm, "mid": v(-35.18, -65.35) * mm, "end": v(-35.5, -65.06) * mm});
            skLineSegment(sketch, "E14.15.30.0", {"start": v(-35.5, -65.06) * mm, "end": v(-35.8, -64.9) * mm});
            skArc(sketch, "E14.18.30.0", {"start": v(-35.8, -64.9) * mm, "mid": v(-36.21, -64.79) * mm, "end": v(-36.63, -64.92) * mm});
            skArc(sketch, "E14.22.30.0", {"start": v(-38.1, -66) * mm, "mid": v(-37.38, -65.44) * mm, "end": v(-36.63, -64.92) * mm});
            skLineSegment(sketch, "E14.26.30.0", {"start": v(-38.1, -66) * mm, "end": v(-38.76, -67.14) * mm});
            skArc(sketch, "E14.29.30.0", {"start": v(-39.85, -67.42) * mm, "mid": v(-39.24, -67.5) * mm, "end": v(-38.76, -67.14) * mm});
            skArc(sketch, "E14.1.31.0", {"start": v(-29.67, -71.62) * mm, "mid": v(-29.67, -72.23) * mm, "end": v(-29.23, -72.66) * mm});
            skLineSegment(sketch, "E14.4.31.0", {"start": v(-29.16, -70.4) * mm, "end": v(-29.67, -71.62) * mm});
            skArc(sketch, "E14.7.31.0", {"start": v(-29.16, -70.4) * mm, "mid": v(-29.16, -69.5) * mm, "end": v(-29.2, -68.58) * mm});
            skArc(sketch, "E14.11.31.0", {"start": v(-29.2, -68.58) * mm, "mid": v(-29.35, -68.17) * mm, "end": v(-29.7, -67.9) * mm});
            skLineSegment(sketch, "E14.15.31.0", {"start": v(-29.7, -67.9) * mm, "end": v(-30, -67.77) * mm});
            skArc(sketch, "E14.18.31.0", {"start": v(-30, -67.77) * mm, "mid": v(-30.43, -67.7) * mm, "end": v(-30.84, -67.86) * mm});
            skArc(sketch, "E14.22.31.0", {"start": v(-32.2, -69.06) * mm, "mid": v(-31.53, -68.45) * mm, "end": v(-30.84, -67.86) * mm});
            skLineSegment(sketch, "E14.26.31.0", {"start": v(-32.2, -69.06) * mm, "end": v(-32.76, -70.26) * mm});
            skArc(sketch, "E14.29.31.0", {"start": v(-33.82, -70.64) * mm, "mid": v(-33.21, -70.67) * mm, "end": v(-32.76, -70.26) * mm});
            skArc(sketch, "E14.1.32.0", {"start": v(-23.31, -73.94) * mm, "mid": v(-23.26, -74.54) * mm, "end": v(-22.8, -74.93) * mm});
            skLineSegment(sketch, "E14.4.32.0", {"start": v(-22.91, -72.67) * mm, "end": v(-23.31, -73.94) * mm});
            skArc(sketch, "E14.7.32.0", {"start": v(-22.91, -72.67) * mm, "mid": v(-23, -71.77) * mm, "end": v(-23.11, -70.87) * mm});
            skArc(sketch, "E14.11.32.0", {"start": v(-23.11, -70.87) * mm, "mid": v(-23.3, -70.47) * mm, "end": v(-23.67, -70.23) * mm});
            skLineSegment(sketch, "E14.15.32.0", {"start": v(-23.67, -70.23) * mm, "end": v(-23.98, -70.13) * mm});
            skArc(sketch, "E14.18.32.0", {"start": v(-23.98, -70.13) * mm, "mid": v(-24.41, -70.1) * mm, "end": v(-24.8, -70.3) * mm});
            skArc(sketch, "E14.22.32.0", {"start": v(-26.06, -71.6) * mm, "mid": v(-25.45, -70.93) * mm, "end": v(-24.8, -70.3) * mm});
            skLineSegment(sketch, "E14.26.32.0", {"start": v(-26.06, -71.6) * mm, "end": v(-26.52, -72.85) * mm});
            skArc(sketch, "E14.29.32.0", {"start": v(-27.53, -73.32) * mm, "mid": v(-26.93, -73.3) * mm, "end": v(-26.52, -72.85) * mm});
            skArc(sketch, "E14.1.33.0", {"start": v(-16.78, -75.69) * mm, "mid": v(-16.67, -76.28) * mm, "end": v(-16.17, -76.63) * mm});
            skLineSegment(sketch, "E14.4.33.0", {"start": v(-16.5, -74.4) * mm, "end": v(-16.78, -75.69) * mm});
            skArc(sketch, "E14.7.33.0", {"start": v(-16.5, -74.4) * mm, "mid": v(-16.65, -73.5) * mm, "end": v(-16.85, -72.61) * mm});
            skArc(sketch, "E14.11.33.0", {"start": v(-16.85, -72.61) * mm, "mid": v(-17.07, -72.23) * mm, "end": v(-17.46, -72.03) * mm});
            skLineSegment(sketch, "E14.15.33.0", {"start": v(-17.46, -72.03) * mm, "end": v(-17.77, -71.95) * mm});
            skArc(sketch, "E14.18.33.0", {"start": v(-17.77, -71.95) * mm, "mid": v(-18.21, -71.95) * mm, "end": v(-18.58, -72.19) * mm});
            skArc(sketch, "E14.22.33.0", {"start": v(-19.72, -73.6) * mm, "mid": v(-19.17, -72.88) * mm, "end": v(-18.58, -72.19) * mm});
            skLineSegment(sketch, "E14.26.33.0", {"start": v(-19.72, -73.6) * mm, "end": v(-20.07, -74.88) * mm});
            skArc(sketch, "E14.29.33.0", {"start": v(-21.04, -75.44) * mm, "mid": v(-20.44, -75.36) * mm, "end": v(-20.07, -74.88) * mm});
            skArc(sketch, "E14.1.34.0", {"start": v(-10.12, -76.86) * mm, "mid": v(-9.96, -77.45) * mm, "end": v(-9.43, -77.75) * mm});
            skLineSegment(sketch, "E14.4.34.0", {"start": v(-9.95, -75.55) * mm, "end": v(-10.12, -76.86) * mm});
            skArc(sketch, "E14.7.34.0", {"start": v(-9.95, -75.55) * mm, "mid": v(-10.18, -74.67) * mm, "end": v(-10.46, -73.8) * mm});
            skArc(sketch, "E14.11.34.0", {"start": v(-10.46, -73.8) * mm, "mid": v(-10.7, -73.44) * mm, "end": v(-11.11, -73.28) * mm});
            skLineSegment(sketch, "E14.15.34.0", {"start": v(-11.11, -73.28) * mm, "end": v(-11.43, -73.23) * mm});
            skArc(sketch, "E14.18.34.0", {"start": v(-11.43, -73.23) * mm, "mid": v(-11.87, -73.26) * mm, "end": v(-12.22, -73.53) * mm});
            skArc(sketch, "E14.22.34.0", {"start": v(-13.23, -75.04) * mm, "mid": v(-12.74, -74.27) * mm, "end": v(-12.22, -73.53) * mm});
            skLineSegment(sketch, "E14.26.34.0", {"start": v(-13.23, -75.04) * mm, "end": v(-13.46, -76.35) * mm});
            skArc(sketch, "E14.29.34.0", {"start": v(-14.38, -76.98) * mm, "mid": v(-13.79, -76.86) * mm, "end": v(-13.46, -76.35) * mm});
            skArc(sketch, "E14.1.35.0", {"start": v(-3.38, -77.45) * mm, "mid": v(-3.17, -78.02) * mm, "end": v(-2.62, -78.27) * mm});
            skLineSegment(sketch, "E14.4.35.0", {"start": v(-3.32, -76.13) * mm, "end": v(-3.38, -77.45) * mm});
            skArc(sketch, "E14.7.35.0", {"start": v(-3.32, -76.13) * mm, "mid": v(-3.63, -75.27) * mm, "end": v(-3.98, -74.43) * mm});
            skArc(sketch, "E14.11.35.0", {"start": v(-3.98, -74.43) * mm, "mid": v(-4.27, -74.1) * mm, "end": v(-4.69, -73.97) * mm});
            skLineSegment(sketch, "E14.15.35.0", {"start": v(-4.69, -73.97) * mm, "end": v(-5, -73.94) * mm});
            skArc(sketch, "E14.18.35.0", {"start": v(-5, -73.94) * mm, "mid": v(-5.44, -74.02) * mm, "end": v(-5.77, -74.32) * mm});
            skArc(sketch, "E14.22.35.0", {"start": v(-6.64, -75.91) * mm, "mid": v(-6.22, -75.1) * mm, "end": v(-5.77, -74.32) * mm});
            skLineSegment(sketch, "E14.26.35.0", {"start": v(-6.64, -75.91) * mm, "end": v(-6.76, -77.23) * mm});
            skArc(sketch, "E14.29.35.0", {"start": v(-7.62, -77.95) * mm, "mid": v(-7.04, -77.77) * mm, "end": v(-6.76, -77.23) * mm});
            skArc(sketch, "E14.1.36.0", {"start": v(3.38, -77.45) * mm, "mid": v(3.64, -78) * mm, "end": v(4.21, -78.2) * mm});
            skLineSegment(sketch, "E14.4.36.0", {"start": v(3.32, -76.13) * mm, "end": v(3.38, -77.45) * mm});
            skArc(sketch, "E14.7.36.0", {"start": v(3.32, -76.13) * mm, "mid": v(2.94, -75.3) * mm, "end": v(2.52, -74.5) * mm});
            skArc(sketch, "E14.11.36.0", {"start": v(2.52, -74.5) * mm, "mid": v(2.2, -74.19) * mm, "end": v(1.78, -74.1) * mm});
            skLineSegment(sketch, "E14.15.36.0", {"start": v(1.78, -74.1) * mm, "end": v(1.45, -74.1) * mm});
            skArc(sketch, "E14.18.36.0", {"start": v(1.45, -74.1) * mm, "mid": v(1.03, -74.21) * mm, "end": v(0.73, -74.54) * mm});
            skArc(sketch, "E14.22.36.0", {"start": v(0, -76.2) * mm, "mid": v(0.35, -75.36) * mm, "end": v(0.73, -74.54) * mm});
            skLineSegment(sketch, "E14.26.36.0", {"start": v(0, -76.2) * mm, "end": v(0, -77.53) * mm});
            skArc(sketch, "E14.29.36.0", {"start": v(-0.8, -78.31) * mm, "mid": v(-0.23, -78.08) * mm, "end": v(0, -77.53) * mm});
            skArc(sketch, "E14.1.37.0", {"start": v(10.12, -76.86) * mm, "mid": v(10.42, -77.39) * mm, "end": v(11.01, -77.54) * mm});
            skLineSegment(sketch, "E14.4.37.0", {"start": v(9.95, -75.55) * mm, "end": v(10.12, -76.86) * mm});
            skArc(sketch, "E14.7.37.0", {"start": v(9.95, -75.55) * mm, "mid": v(9.5, -74.76) * mm, "end": v(9, -74) * mm});
            skArc(sketch, "E14.11.37.0", {"start": v(9, -74) * mm, "mid": v(8.66, -73.71) * mm, "end": v(8.23, -73.66) * mm});
            skLineSegment(sketch, "E14.15.37.0", {"start": v(8.23, -73.66) * mm, "end": v(7.9, -73.7) * mm});
            skArc(sketch, "E14.18.37.0", {"start": v(7.9, -73.7) * mm, "mid": v(7.5, -73.84) * mm, "end": v(7.23, -74.19) * mm});
            skArc(sketch, "E14.22.37.0", {"start": v(6.64, -75.91) * mm, "mid": v(6.91, -75.04) * mm, "end": v(7.23, -74.19) * mm});
            skLineSegment(sketch, "E14.26.37.0", {"start": v(6.64, -75.91) * mm, "end": v(6.76, -77.23) * mm});
            skArc(sketch, "E14.29.37.0", {"start": v(6.03, -78.08) * mm, "mid": v(6.57, -77.8) * mm, "end": v(6.76, -77.23) * mm});
            skArc(sketch, "E14.1.38.0", {"start": v(16.78, -75.69) * mm, "mid": v(17.13, -76.18) * mm, "end": v(17.73, -76.28) * mm});
            skLineSegment(sketch, "E14.4.38.0", {"start": v(16.5, -74.4) * mm, "end": v(16.78, -75.69) * mm});
            skArc(sketch, "E14.7.38.0", {"start": v(16.5, -74.4) * mm, "mid": v(15.97, -73.65) * mm, "end": v(15.42, -72.93) * mm});
            skArc(sketch, "E14.11.38.0", {"start": v(15.42, -72.93) * mm, "mid": v(15.06, -72.68) * mm, "end": v(14.62, -72.66) * mm});
            skLineSegment(sketch, "E14.15.38.0", {"start": v(14.62, -72.66) * mm, "end": v(14.3, -72.72) * mm});
            skArc(sketch, "E14.18.38.0", {"start": v(14.3, -72.72) * mm, "mid": v(13.9, -72.9) * mm, "end": v(13.66, -73.28) * mm});
            skArc(sketch, "E14.22.38.0", {"start": v(13.23, -75.04) * mm, "mid": v(13.43, -74.15) * mm, "end": v(13.66, -73.28) * mm});
            skLineSegment(sketch, "E14.26.38.0", {"start": v(13.23, -75.04) * mm, "end": v(13.46, -76.35) * mm});
            skArc(sketch, "E14.29.38.0", {"start": v(12.82, -77.26) * mm, "mid": v(13.33, -76.94) * mm, "end": v(13.46, -76.35) * mm});
            skArc(sketch, "E14.1.39.0", {"start": v(23.31, -73.94) * mm, "mid": v(23.7, -74.4) * mm, "end": v(24.3, -74.45) * mm});
            skLineSegment(sketch, "E14.4.39.0", {"start": v(22.91, -72.67) * mm, "end": v(23.31, -73.94) * mm});
            skArc(sketch, "E14.7.39.0", {"start": v(22.91, -72.67) * mm, "mid": v(22.33, -71.98) * mm, "end": v(21.71, -71.3) * mm});
            skArc(sketch, "E14.11.39.0", {"start": v(21.71, -71.3) * mm, "mid": v(21.33, -71.09) * mm, "end": v(20.9, -71.1) * mm});
            skLineSegment(sketch, "E14.15.39.0", {"start": v(20.9, -71.1) * mm, "end": v(20.58, -71.2) * mm});
            skArc(sketch, "E14.18.39.0", {"start": v(20.58, -71.2) * mm, "mid": v(20.2, -71.42) * mm, "end": v(20, -71.8) * mm});
            skArc(sketch, "E14.22.39.0", {"start": v(19.72, -73.6) * mm, "mid": v(19.84, -72.7) * mm, "end": v(20, -71.8) * mm});
            skLineSegment(sketch, "E14.26.39.0", {"start": v(19.72, -73.6) * mm, "end": v(20.07, -74.88) * mm});
            skArc(sketch, "E14.29.39.0", {"start": v(19.5, -75.85) * mm, "mid": v(19.98, -75.48) * mm, "end": v(20.07, -74.88) * mm});
            skArc(sketch, "E14.1.40.0", {"start": v(29.67, -71.62) * mm, "mid": v(30.1, -72.05) * mm, "end": v(30.7, -72.05) * mm});
            skLineSegment(sketch, "E14.4.40.0", {"start": v(29.16, -70.4) * mm, "end": v(29.67, -71.62) * mm});
            skArc(sketch, "E14.7.40.0", {"start": v(29.16, -70.4) * mm, "mid": v(28.52, -69.76) * mm, "end": v(27.85, -69.14) * mm});
            skArc(sketch, "E14.11.40.0", {"start": v(27.85, -69.14) * mm, "mid": v(27.45, -68.96) * mm, "end": v(27.01, -69.02) * mm});
            skLineSegment(sketch, "E14.15.40.0", {"start": v(27.01, -69.02) * mm, "end": v(26.71, -69.13) * mm});
            skArc(sketch, "E14.18.40.0", {"start": v(26.71, -69.13) * mm, "mid": v(26.35, -69.39) * mm, "end": v(26.18, -69.79) * mm});
            skArc(sketch, "E14.22.40.0", {"start": v(26.06, -71.6) * mm, "mid": v(26.1, -70.7) * mm, "end": v(26.18, -69.79) * mm});
            skLineSegment(sketch, "E14.26.40.0", {"start": v(26.06, -71.6) * mm, "end": v(26.52, -72.85) * mm});
            skArc(sketch, "E14.29.40.0", {"start": v(26.04, -73.86) * mm, "mid": v(26.49, -73.46) * mm, "end": v(26.52, -72.85) * mm});
            skArc(sketch, "E14.1.41.0", {"start": v(35.8, -68.77) * mm, "mid": v(36.26, -69.15) * mm, "end": v(36.87, -69.1) * mm});
            skLineSegment(sketch, "E14.4.41.0", {"start": v(35.19, -67.6) * mm, "end": v(35.8, -68.77) * mm});
            skArc(sketch, "E14.7.41.0", {"start": v(35.19, -67.6) * mm, "mid": v(34.49, -67) * mm, "end": v(33.77, -66.45) * mm});
            skArc(sketch, "E14.11.41.0", {"start": v(33.77, -66.45) * mm, "mid": v(33.35, -66.3) * mm, "end": v(32.93, -66.4) * mm});
            skLineSegment(sketch, "E14.15.41.0", {"start": v(32.93, -66.4) * mm, "end": v(32.63, -66.54) * mm});
            skArc(sketch, "E14.18.41.0", {"start": v(32.63, -66.54) * mm, "mid": v(32.3, -66.82) * mm, "end": v(32.16, -67.24) * mm});
            skArc(sketch, "E14.22.41.0", {"start": v(32.2, -69.06) * mm, "mid": v(32.16, -68.15) * mm, "end": v(32.16, -67.24) * mm});
            skLineSegment(sketch, "E14.26.41.0", {"start": v(32.2, -69.06) * mm, "end": v(32.76, -70.26) * mm});
            skArc(sketch, "E14.29.41.0", {"start": v(32.38, -71.31) * mm, "mid": v(32.79, -70.87) * mm, "end": v(32.76, -70.26) * mm});
            skArc(sketch, "E14.1.42.0", {"start": v(41.65, -65.38) * mm, "mid": v(42.15, -65.73) * mm, "end": v(42.75, -65.62) * mm});
            skLineSegment(sketch, "E14.4.42.0", {"start": v(40.94, -64.27) * mm, "end": v(41.65, -65.38) * mm});
            skArc(sketch, "E14.7.42.0", {"start": v(40.94, -64.27) * mm, "mid": v(40.2, -63.74) * mm, "end": v(39.43, -63.26) * mm});
            skArc(sketch, "E14.11.42.0", {"start": v(39.43, -63.26) * mm, "mid": v(39, -63.14) * mm, "end": v(38.59, -63.28) * mm});
            skLineSegment(sketch, "E14.15.42.0", {"start": v(38.59, -63.28) * mm, "end": v(38.3, -63.45) * mm});
            skArc(sketch, "E14.18.42.0", {"start": v(38.3, -63.45) * mm, "mid": v(38, -63.76) * mm, "end": v(37.9, -64.18) * mm});
            skArc(sketch, "E14.22.42.0", {"start": v(38.1, -66) * mm, "mid": v(37.98, -65.09) * mm, "end": v(37.9, -64.18) * mm});
            skLineSegment(sketch, "E14.26.42.0", {"start": v(38.1, -66) * mm, "end": v(38.76, -67.14) * mm});
            skArc(sketch, "E14.29.42.0", {"start": v(38.47, -68.22) * mm, "mid": v(38.84, -67.74) * mm, "end": v(38.76, -67.14) * mm});
            skArc(sketch, "E14.1.43.0", {"start": v(47.2, -61.5) * mm, "mid": v(47.72, -61.8) * mm, "end": v(48.3, -61.65) * mm});
            skLineSegment(sketch, "E14.4.43.0", {"start": v(46.39, -60.45) * mm, "end": v(47.2, -61.5) * mm});
            skArc(sketch, "E14.7.43.0", {"start": v(46.39, -60.45) * mm, "mid": v(45.6, -60) * mm, "end": v(44.8, -59.58) * mm});
            skArc(sketch, "E14.11.43.0", {"start": v(44.8, -59.58) * mm, "mid": v(44.36, -59.5) * mm, "end": v(43.96, -59.67) * mm});
            skLineSegment(sketch, "E14.15.43.0", {"start": v(43.96, -59.67) * mm, "end": v(43.7, -59.86) * mm});
            skArc(sketch, "E14.18.43.0", {"start": v(43.7, -59.86) * mm, "mid": v(43.41, -60.2) * mm, "end": v(43.35, -60.64) * mm});
            skArc(sketch, "E14.22.43.0", {"start": v(43.7, -62.42) * mm, "mid": v(43.5, -61.53) * mm, "end": v(43.35, -60.64) * mm});
            skLineSegment(sketch, "E14.26.43.0", {"start": v(43.7, -62.42) * mm, "end": v(44.47, -63.5) * mm});
            skArc(sketch, "E14.29.43.0", {"start": v(44.27, -64.6) * mm, "mid": v(44.6, -64.1) * mm, "end": v(44.47, -63.5) * mm});
            skArc(sketch, "E14.1.44.0", {"start": v(52.38, -57.16) * mm, "mid": v(52.93, -57.41) * mm, "end": v(53.5, -57.2) * mm});
            skLineSegment(sketch, "E14.4.44.0", {"start": v(51.48, -56.18) * mm, "end": v(52.38, -57.16) * mm});
            skArc(sketch, "E14.7.44.0", {"start": v(51.48, -56.18) * mm, "mid": v(50.66, -55.8) * mm, "end": v(49.82, -55.45) * mm});
            skArc(sketch, "E14.11.44.0", {"start": v(49.82, -55.45) * mm, "mid": v(49.38, -55.41) * mm, "end": v(48.99, -55.62) * mm});
            skLineSegment(sketch, "E14.15.44.0", {"start": v(48.99, -55.62) * mm, "end": v(48.75, -55.83) * mm});
            skArc(sketch, "E14.18.44.0", {"start": v(48.75, -55.83) * mm, "mid": v(48.5, -56.19) * mm, "end": v(48.47, -56.63) * mm});
            skArc(sketch, "E14.22.44.0", {"start": v(48.98, -58.37) * mm, "mid": v(48.7, -57.5) * mm, "end": v(48.47, -56.63) * mm});
            skLineSegment(sketch, "E14.26.44.0", {"start": v(48.98, -58.37) * mm, "end": v(49.83, -59.39) * mm});
            skArc(sketch, "E14.29.44.0", {"start": v(49.73, -60.5) * mm, "mid": v(50.01, -59.97) * mm, "end": v(49.83, -59.39) * mm});
            skArc(sketch, "E14.1.45.0", {"start": v(57.16, -52.38) * mm, "mid": v(57.73, -52.58) * mm, "end": v(58.28, -52.32) * mm});
            skLineSegment(sketch, "E14.4.45.0", {"start": v(56.18, -51.48) * mm, "end": v(57.16, -52.38) * mm});
            skArc(sketch, "E14.7.45.0", {"start": v(56.18, -51.48) * mm, "mid": v(55.33, -51.17) * mm, "end": v(54.46, -50.9) * mm});
            skArc(sketch, "E14.11.45.0", {"start": v(54.46, -50.9) * mm, "mid": v(54.02, -50.9) * mm, "end": v(53.65, -51.13) * mm});
            skLineSegment(sketch, "E14.15.45.0", {"start": v(53.65, -51.13) * mm, "end": v(53.43, -51.37) * mm});
            skArc(sketch, "E14.18.45.0", {"start": v(53.43, -51.37) * mm, "mid": v(53.2, -51.75) * mm, "end": v(53.22, -52.19) * mm});
            skArc(sketch, "E14.22.45.0", {"start": v(53.88, -53.88) * mm, "mid": v(53.53, -53.04) * mm, "end": v(53.22, -52.19) * mm});
            skLineSegment(sketch, "E14.26.45.0", {"start": v(53.88, -53.88) * mm, "end": v(54.82, -54.82) * mm});
            skArc(sketch, "E14.29.45.0", {"start": v(54.81, -55.94) * mm, "mid": v(55.05, -55.38) * mm, "end": v(54.82, -54.82) * mm});
            skArc(sketch, "E14.1.46.0", {"start": v(61.5, -47.2) * mm, "mid": v(62.1, -47.35) * mm, "end": v(62.61, -47.04) * mm});
            skLineSegment(sketch, "E14.4.46.0", {"start": v(60.45, -46.39) * mm, "end": v(61.5, -47.2) * mm});
            skArc(sketch, "E14.7.46.0", {"start": v(60.45, -46.39) * mm, "mid": v(59.58, -46.15) * mm, "end": v(58.69, -45.96) * mm});
            skArc(sketch, "E14.11.46.0", {"start": v(58.69, -45.96) * mm, "mid": v(58.25, -46) * mm, "end": v(57.9, -46.26) * mm});
            skLineSegment(sketch, "E14.15.46.0", {"start": v(57.9, -46.26) * mm, "end": v(57.7, -46.52) * mm});
            skArc(sketch, "E14.18.46.0", {"start": v(57.7, -46.52) * mm, "mid": v(57.51, -46.91) * mm, "end": v(57.57, -47.35) * mm});
            skArc(sketch, "E14.22.46.0", {"start": v(58.37, -48.98) * mm, "mid": v(57.95, -48.17) * mm, "end": v(57.57, -47.35) * mm});
            skLineSegment(sketch, "E14.26.46.0", {"start": v(58.37, -48.98) * mm, "end": v(59.39, -49.83) * mm});
            skArc(sketch, "E14.29.46.0", {"start": v(59.48, -50.95) * mm, "mid": v(59.67, -50.37) * mm, "end": v(59.39, -49.83) * mm});
            skArc(sketch, "E14.1.47.0", {"start": v(65.38, -41.65) * mm, "mid": v(65.98, -41.76) * mm, "end": v(66.48, -41.4) * mm});
            skLineSegment(sketch, "E14.4.47.0", {"start": v(64.27, -40.94) * mm, "end": v(65.38, -41.65) * mm});
            skArc(sketch, "E14.7.47.0", {"start": v(64.27, -40.94) * mm, "mid": v(63.37, -40.78) * mm, "end": v(62.47, -40.67) * mm});
            skArc(sketch, "E14.11.47.0", {"start": v(62.47, -40.67) * mm, "mid": v(62.04, -40.74) * mm, "end": v(61.71, -41.04) * mm});
            skLineSegment(sketch, "E14.15.47.0", {"start": v(61.71, -41.04) * mm, "end": v(61.53, -41.31) * mm});
            skArc(sketch, "E14.18.47.0", {"start": v(61.53, -41.31) * mm, "mid": v(61.38, -41.72) * mm, "end": v(61.48, -42.15) * mm});
            skArc(sketch, "E14.22.47.0", {"start": v(62.42, -43.7) * mm, "mid": v(61.93, -42.94) * mm, "end": v(61.48, -42.15) * mm});
            skLineSegment(sketch, "E14.26.47.0", {"start": v(62.42, -43.7) * mm, "end": v(63.5, -44.47) * mm});
            skArc(sketch, "E14.29.47.0", {"start": v(63.7, -45.57) * mm, "mid": v(63.83, -44.98) * mm, "end": v(63.5, -44.47) * mm});
            skArc(sketch, "E14.1.48.0", {"start": v(68.77, -35.8) * mm, "mid": v(69.37, -35.85) * mm, "end": v(69.83, -35.46) * mm});
            skLineSegment(sketch, "E14.4.48.0", {"start": v(67.6, -35.19) * mm, "end": v(68.77, -35.8) * mm});
            skArc(sketch, "E14.7.48.0", {"start": v(67.6, -35.19) * mm, "mid": v(66.68, -35.1) * mm, "end": v(65.78, -35.07) * mm});
            skArc(sketch, "E14.11.48.0", {"start": v(65.78, -35.07) * mm, "mid": v(65.35, -35.18) * mm, "end": v(65.06, -35.5) * mm});
            skLineSegment(sketch, "E14.15.48.0", {"start": v(65.06, -35.5) * mm, "end": v(64.9, -35.8) * mm});
            skArc(sketch, "E14.18.48.0", {"start": v(64.9, -35.8) * mm, "mid": v(64.79, -36.21) * mm, "end": v(64.92, -36.63) * mm});
            skArc(sketch, "E14.22.48.0", {"start": v(66, -38.1) * mm, "mid": v(65.44, -37.38) * mm, "end": v(64.92, -36.63) * mm});
            skLineSegment(sketch, "E14.26.48.0", {"start": v(66, -38.1) * mm, "end": v(67.14, -38.76) * mm});
            skArc(sketch, "E14.29.48.0", {"start": v(67.42, -39.85) * mm, "mid": v(67.5, -39.24) * mm, "end": v(67.14, -38.76) * mm});
            skArc(sketch, "E14.1.49.0", {"start": v(71.62, -29.67) * mm, "mid": v(72.23, -29.67) * mm, "end": v(72.66, -29.23) * mm});
            skLineSegment(sketch, "E14.4.49.0", {"start": v(70.4, -29.16) * mm, "end": v(71.62, -29.67) * mm});
            skArc(sketch, "E14.7.49.0", {"start": v(70.4, -29.16) * mm, "mid": v(69.5, -29.16) * mm, "end": v(68.58, -29.2) * mm});
            skArc(sketch, "E14.11.49.0", {"start": v(68.58, -29.2) * mm, "mid": v(68.17, -29.35) * mm, "end": v(67.9, -29.7) * mm});
            skLineSegment(sketch, "E14.15.49.0", {"start": v(67.9, -29.7) * mm, "end": v(67.77, -30) * mm});
            skArc(sketch, "E14.18.49.0", {"start": v(67.77, -30) * mm, "mid": v(67.7, -30.43) * mm, "end": v(67.86, -30.84) * mm});
            skArc(sketch, "E14.22.49.0", {"start": v(69.06, -32.2) * mm, "mid": v(68.45, -31.53) * mm, "end": v(67.86, -30.84) * mm});
            skLineSegment(sketch, "E14.26.49.0", {"start": v(69.06, -32.2) * mm, "end": v(70.26, -32.76) * mm});
            skArc(sketch, "E14.29.49.0", {"start": v(70.64, -33.82) * mm, "mid": v(70.67, -33.21) * mm, "end": v(70.26, -32.76) * mm});
            skArc(sketch, "E14.1.50.0", {"start": v(73.94, -23.31) * mm, "mid": v(74.54, -23.26) * mm, "end": v(74.93, -22.8) * mm});
            skLineSegment(sketch, "E14.4.50.0", {"start": v(72.67, -22.91) * mm, "end": v(73.94, -23.31) * mm});
            skArc(sketch, "E14.7.50.0", {"start": v(72.67, -22.91) * mm, "mid": v(71.77, -23) * mm, "end": v(70.87, -23.11) * mm});
            skArc(sketch, "E14.11.50.0", {"start": v(70.87, -23.11) * mm, "mid": v(70.47, -23.3) * mm, "end": v(70.23, -23.67) * mm});
            skLineSegment(sketch, "E14.15.50.0", {"start": v(70.23, -23.67) * mm, "end": v(70.13, -23.98) * mm});
            skArc(sketch, "E14.18.50.0", {"start": v(70.13, -23.98) * mm, "mid": v(70.1, -24.41) * mm, "end": v(70.3, -24.8) * mm});
            skArc(sketch, "E14.22.50.0", {"start": v(71.6, -26.06) * mm, "mid": v(70.93, -25.45) * mm, "end": v(70.3, -24.8) * mm});
            skLineSegment(sketch, "E14.26.50.0", {"start": v(71.6, -26.06) * mm, "end": v(72.85, -26.52) * mm});
            skArc(sketch, "E14.29.50.0", {"start": v(73.32, -27.53) * mm, "mid": v(73.3, -26.93) * mm, "end": v(72.85, -26.52) * mm});
            skArc(sketch, "E14.1.51.0", {"start": v(75.69, -16.78) * mm, "mid": v(76.28, -16.67) * mm, "end": v(76.63, -16.17) * mm});
            skLineSegment(sketch, "E14.4.51.0", {"start": v(74.4, -16.5) * mm, "end": v(75.69, -16.78) * mm});
            skArc(sketch, "E14.7.51.0", {"start": v(74.4, -16.5) * mm, "mid": v(73.5, -16.65) * mm, "end": v(72.61, -16.85) * mm});
            skArc(sketch, "E14.11.51.0", {"start": v(72.61, -16.85) * mm, "mid": v(72.23, -17.07) * mm, "end": v(72.03, -17.46) * mm});
            skLineSegment(sketch, "E14.15.51.0", {"start": v(72.03, -17.46) * mm, "end": v(71.95, -17.77) * mm});
            skArc(sketch, "E14.18.51.0", {"start": v(71.95, -17.77) * mm, "mid": v(71.95, -18.21) * mm, "end": v(72.19, -18.58) * mm});
            skArc(sketch, "E14.22.51.0", {"start": v(73.6, -19.72) * mm, "mid": v(72.88, -19.17) * mm, "end": v(72.19, -18.58) * mm});
            skLineSegment(sketch, "E14.26.51.0", {"start": v(73.6, -19.72) * mm, "end": v(74.88, -20.07) * mm});
            skArc(sketch, "E14.29.51.0", {"start": v(75.44, -21.04) * mm, "mid": v(75.36, -20.44) * mm, "end": v(74.88, -20.07) * mm});
            skArc(sketch, "E14.1.52.0", {"start": v(76.86, -10.12) * mm, "mid": v(77.45, -9.96) * mm, "end": v(77.75, -9.43) * mm});
            skLineSegment(sketch, "E14.4.52.0", {"start": v(75.55, -9.95) * mm, "end": v(76.86, -10.12) * mm});
            skArc(sketch, "E14.7.52.0", {"start": v(75.55, -9.95) * mm, "mid": v(74.67, -10.18) * mm, "end": v(73.8, -10.46) * mm});
            skArc(sketch, "E14.11.52.0", {"start": v(73.8, -10.46) * mm, "mid": v(73.44, -10.7) * mm, "end": v(73.28, -11.11) * mm});
            skLineSegment(sketch, "E14.15.52.0", {"start": v(73.28, -11.11) * mm, "end": v(73.23, -11.43) * mm});
            skArc(sketch, "E14.18.52.0", {"start": v(73.23, -11.43) * mm, "mid": v(73.26, -11.87) * mm, "end": v(73.53, -12.22) * mm});
            skArc(sketch, "E14.22.52.0", {"start": v(75.04, -13.23) * mm, "mid": v(74.27, -12.74) * mm, "end": v(73.53, -12.22) * mm});
            skLineSegment(sketch, "E14.26.52.0", {"start": v(75.04, -13.23) * mm, "end": v(76.35, -13.46) * mm});
            skArc(sketch, "E14.29.52.0", {"start": v(76.98, -14.38) * mm, "mid": v(76.86, -13.79) * mm, "end": v(76.35, -13.46) * mm});
            skArc(sketch, "E14.1.53.0", {"start": v(77.45, -3.38) * mm, "mid": v(78.02, -3.17) * mm, "end": v(78.27, -2.62) * mm});
            skLineSegment(sketch, "E14.4.53.0", {"start": v(76.13, -3.32) * mm, "end": v(77.45, -3.38) * mm});
            skArc(sketch, "E14.7.53.0", {"start": v(76.13, -3.32) * mm, "mid": v(75.27, -3.63) * mm, "end": v(74.43, -3.98) * mm});
            skArc(sketch, "E14.11.53.0", {"start": v(74.43, -3.98) * mm, "mid": v(74.1, -4.27) * mm, "end": v(73.97, -4.69) * mm});
            skLineSegment(sketch, "E14.15.53.0", {"start": v(73.97, -4.69) * mm, "end": v(73.94, -5) * mm});
            skArc(sketch, "E14.18.53.0", {"start": v(73.94, -5) * mm, "mid": v(74.02, -5.44) * mm, "end": v(74.32, -5.77) * mm});
            skArc(sketch, "E14.22.53.0", {"start": v(75.91, -6.64) * mm, "mid": v(75.1, -6.22) * mm, "end": v(74.32, -5.77) * mm});
            skLineSegment(sketch, "E14.26.53.0", {"start": v(75.91, -6.64) * mm, "end": v(77.23, -6.76) * mm});
            skArc(sketch, "E14.29.53.0", {"start": v(77.95, -7.62) * mm, "mid": v(77.77, -7.04) * mm, "end": v(77.23, -6.76) * mm});
            skArc(sketch, "E14.1.54.0", {"start": v(77.45, 3.38) * mm, "mid": v(78, 3.64) * mm, "end": v(78.2, 4.21) * mm});
            skLineSegment(sketch, "E14.4.54.0", {"start": v(76.13, 3.32) * mm, "end": v(77.45, 3.38) * mm});
            skArc(sketch, "E14.7.54.0", {"start": v(76.13, 3.32) * mm, "mid": v(75.3, 2.94) * mm, "end": v(74.5, 2.52) * mm});
            skArc(sketch, "E14.11.54.0", {"start": v(74.5, 2.52) * mm, "mid": v(74.19, 2.2) * mm, "end": v(74.1, 1.78) * mm});
            skLineSegment(sketch, "E14.15.54.0", {"start": v(74.1, 1.78) * mm, "end": v(74.1, 1.45) * mm});
            skArc(sketch, "E14.18.54.0", {"start": v(74.1, 1.45) * mm, "mid": v(74.21, 1.03) * mm, "end": v(74.54, 0.73) * mm});
            skArc(sketch, "E14.22.54.0", {"start": v(76.2, 0) * mm, "mid": v(75.36, 0.35) * mm, "end": v(74.54, 0.73) * mm});
            skLineSegment(sketch, "E14.26.54.0", {"start": v(76.2, 0) * mm, "end": v(77.53, 0) * mm});
            skArc(sketch, "E14.29.54.0", {"start": v(78.31, -0.8) * mm, "mid": v(78.08, -0.23) * mm, "end": v(77.53, 0) * mm});
            skArc(sketch, "E14.1.55.0", {"start": v(76.86, 10.12) * mm, "mid": v(77.39, 10.42) * mm, "end": v(77.54, 11.01) * mm});
            skLineSegment(sketch, "E14.4.55.0", {"start": v(75.55, 9.95) * mm, "end": v(76.86, 10.12) * mm});
            skArc(sketch, "E14.7.55.0", {"start": v(75.55, 9.95) * mm, "mid": v(74.76, 9.5) * mm, "end": v(74, 9) * mm});
            skArc(sketch, "E14.11.55.0", {"start": v(74, 9) * mm, "mid": v(73.71, 8.66) * mm, "end": v(73.66, 8.23) * mm});
            skLineSegment(sketch, "E14.15.55.0", {"start": v(73.66, 8.23) * mm, "end": v(73.7, 7.9) * mm});
            skArc(sketch, "E14.18.55.0", {"start": v(73.7, 7.9) * mm, "mid": v(73.84, 7.5) * mm, "end": v(74.19, 7.23) * mm});
            skArc(sketch, "E14.22.55.0", {"start": v(75.91, 6.64) * mm, "mid": v(75.04, 6.91) * mm, "end": v(74.19, 7.23) * mm});
            skLineSegment(sketch, "E14.26.55.0", {"start": v(75.91, 6.64) * mm, "end": v(77.23, 6.76) * mm});
            skArc(sketch, "E14.29.55.0", {"start": v(78.08, 6.03) * mm, "mid": v(77.8, 6.57) * mm, "end": v(77.23, 6.76) * mm});
            skArc(sketch, "E14.1.56.0", {"start": v(75.69, 16.78) * mm, "mid": v(76.18, 17.13) * mm, "end": v(76.28, 17.73) * mm});
            skLineSegment(sketch, "E14.4.56.0", {"start": v(74.4, 16.5) * mm, "end": v(75.69, 16.78) * mm});
            skArc(sketch, "E14.7.56.0", {"start": v(74.4, 16.5) * mm, "mid": v(73.65, 15.97) * mm, "end": v(72.93, 15.42) * mm});
            skArc(sketch, "E14.11.56.0", {"start": v(72.93, 15.42) * mm, "mid": v(72.68, 15.06) * mm, "end": v(72.66, 14.62) * mm});
            skLineSegment(sketch, "E14.15.56.0", {"start": v(72.66, 14.62) * mm, "end": v(72.72, 14.3) * mm});
            skArc(sketch, "E14.18.56.0", {"start": v(72.72, 14.3) * mm, "mid": v(72.9, 13.9) * mm, "end": v(73.28, 13.66) * mm});
            skArc(sketch, "E14.22.56.0", {"start": v(75.04, 13.23) * mm, "mid": v(74.15, 13.43) * mm, "end": v(73.28, 13.66) * mm});
            skLineSegment(sketch, "E14.26.56.0", {"start": v(75.04, 13.23) * mm, "end": v(76.35, 13.46) * mm});
            skArc(sketch, "E14.29.56.0", {"start": v(77.26, 12.82) * mm, "mid": v(76.94, 13.33) * mm, "end": v(76.35, 13.46) * mm});
            skArc(sketch, "E14.1.57.0", {"start": v(73.94, 23.31) * mm, "mid": v(74.4, 23.7) * mm, "end": v(74.45, 24.3) * mm});
            skLineSegment(sketch, "E14.4.57.0", {"start": v(72.67, 22.91) * mm, "end": v(73.94, 23.31) * mm});
            skArc(sketch, "E14.7.57.0", {"start": v(72.67, 22.91) * mm, "mid": v(71.98, 22.33) * mm, "end": v(71.3, 21.71) * mm});
            skArc(sketch, "E14.11.57.0", {"start": v(71.3, 21.71) * mm, "mid": v(71.09, 21.33) * mm, "end": v(71.1, 20.9) * mm});
            skLineSegment(sketch, "E14.15.57.0", {"start": v(71.1, 20.9) * mm, "end": v(71.2, 20.58) * mm});
            skArc(sketch, "E14.18.57.0", {"start": v(71.2, 20.58) * mm, "mid": v(71.42, 20.2) * mm, "end": v(71.8, 20) * mm});
            skArc(sketch, "E14.22.57.0", {"start": v(73.6, 19.72) * mm, "mid": v(72.7, 19.84) * mm, "end": v(71.8, 20) * mm});
            skLineSegment(sketch, "E14.26.57.0", {"start": v(73.6, 19.72) * mm, "end": v(74.88, 20.07) * mm});
            skArc(sketch, "E14.29.57.0", {"start": v(75.85, 19.5) * mm, "mid": v(75.48, 19.98) * mm, "end": v(74.88, 20.07) * mm});
            skArc(sketch, "E14.1.58.0", {"start": v(71.62, 29.67) * mm, "mid": v(72.05, 30.1) * mm, "end": v(72.05, 30.7) * mm});
            skLineSegment(sketch, "E14.4.58.0", {"start": v(70.4, 29.16) * mm, "end": v(71.62, 29.67) * mm});
            skArc(sketch, "E14.7.58.0", {"start": v(70.4, 29.16) * mm, "mid": v(69.76, 28.52) * mm, "end": v(69.14, 27.85) * mm});
            skArc(sketch, "E14.11.58.0", {"start": v(69.14, 27.85) * mm, "mid": v(68.96, 27.45) * mm, "end": v(69.02, 27.01) * mm});
            skLineSegment(sketch, "E14.15.58.0", {"start": v(69.02, 27.01) * mm, "end": v(69.13, 26.71) * mm});
            skArc(sketch, "E14.18.58.0", {"start": v(69.13, 26.71) * mm, "mid": v(69.39, 26.35) * mm, "end": v(69.79, 26.18) * mm});
            skArc(sketch, "E14.22.58.0", {"start": v(71.6, 26.06) * mm, "mid": v(70.7, 26.1) * mm, "end": v(69.79, 26.18) * mm});
            skLineSegment(sketch, "E14.26.58.0", {"start": v(71.6, 26.06) * mm, "end": v(72.85, 26.52) * mm});
            skArc(sketch, "E14.29.58.0", {"start": v(73.86, 26.04) * mm, "mid": v(73.46, 26.49) * mm, "end": v(72.85, 26.52) * mm});
            skArc(sketch, "E14.1.59.0", {"start": v(68.77, 35.8) * mm, "mid": v(69.15, 36.26) * mm, "end": v(69.1, 36.87) * mm});
            skLineSegment(sketch, "E14.4.59.0", {"start": v(67.6, 35.19) * mm, "end": v(68.77, 35.8) * mm});
            skArc(sketch, "E14.7.59.0", {"start": v(67.6, 35.19) * mm, "mid": v(67, 34.49) * mm, "end": v(66.45, 33.77) * mm});
            skArc(sketch, "E14.11.59.0", {"start": v(66.45, 33.77) * mm, "mid": v(66.3, 33.35) * mm, "end": v(66.4, 32.93) * mm});
            skLineSegment(sketch, "E14.15.59.0", {"start": v(66.4, 32.93) * mm, "end": v(66.54, 32.63) * mm});
            skArc(sketch, "E14.18.59.0", {"start": v(66.54, 32.63) * mm, "mid": v(66.82, 32.3) * mm, "end": v(67.24, 32.16) * mm});
            skArc(sketch, "E14.22.59.0", {"start": v(69.06, 32.2) * mm, "mid": v(68.15, 32.16) * mm, "end": v(67.24, 32.16) * mm});
            skLineSegment(sketch, "E14.26.59.0", {"start": v(69.06, 32.2) * mm, "end": v(70.26, 32.76) * mm});
            skArc(sketch, "E14.29.59.0", {"start": v(71.31, 32.38) * mm, "mid": v(70.87, 32.79) * mm, "end": v(70.26, 32.76) * mm});
            skArc(sketch, "E14.1.60.0", {"start": v(65.38, 41.65) * mm, "mid": v(65.73, 42.15) * mm, "end": v(65.62, 42.75) * mm});
            skLineSegment(sketch, "E14.4.60.0", {"start": v(64.27, 40.94) * mm, "end": v(65.38, 41.65) * mm});
            skArc(sketch, "E14.7.60.0", {"start": v(64.27, 40.94) * mm, "mid": v(63.74, 40.2) * mm, "end": v(63.26, 39.43) * mm});
            skArc(sketch, "E14.11.60.0", {"start": v(63.26, 39.43) * mm, "mid": v(63.14, 39) * mm, "end": v(63.28, 38.59) * mm});
            skLineSegment(sketch, "E14.15.60.0", {"start": v(63.28, 38.59) * mm, "end": v(63.45, 38.3) * mm});
            skArc(sketch, "E14.18.60.0", {"start": v(63.45, 38.3) * mm, "mid": v(63.76, 38) * mm, "end": v(64.18, 37.9) * mm});
            skArc(sketch, "E14.22.60.0", {"start": v(66, 38.1) * mm, "mid": v(65.09, 37.98) * mm, "end": v(64.18, 37.9) * mm});
            skLineSegment(sketch, "E14.26.60.0", {"start": v(66, 38.1) * mm, "end": v(67.14, 38.76) * mm});
            skArc(sketch, "E14.29.60.0", {"start": v(68.22, 38.47) * mm, "mid": v(67.74, 38.84) * mm, "end": v(67.14, 38.76) * mm});
            skArc(sketch, "E14.1.61.0", {"start": v(61.5, 47.2) * mm, "mid": v(61.8, 47.72) * mm, "end": v(61.65, 48.3) * mm});
            skLineSegment(sketch, "E14.4.61.0", {"start": v(60.45, 46.39) * mm, "end": v(61.5, 47.2) * mm});
            skArc(sketch, "E14.7.61.0", {"start": v(60.45, 46.39) * mm, "mid": v(60, 45.6) * mm, "end": v(59.58, 44.8) * mm});
            skArc(sketch, "E14.11.61.0", {"start": v(59.58, 44.8) * mm, "mid": v(59.5, 44.36) * mm, "end": v(59.67, 43.96) * mm});
            skLineSegment(sketch, "E14.15.61.0", {"start": v(59.67, 43.96) * mm, "end": v(59.86, 43.7) * mm});
            skArc(sketch, "E14.18.61.0", {"start": v(59.86, 43.7) * mm, "mid": v(60.2, 43.41) * mm, "end": v(60.64, 43.35) * mm});
            skArc(sketch, "E14.22.61.0", {"start": v(62.42, 43.7) * mm, "mid": v(61.53, 43.5) * mm, "end": v(60.64, 43.35) * mm});
            skLineSegment(sketch, "E14.26.61.0", {"start": v(62.42, 43.7) * mm, "end": v(63.5, 44.47) * mm});
            skArc(sketch, "E14.29.61.0", {"start": v(64.6, 44.27) * mm, "mid": v(64.1, 44.6) * mm, "end": v(63.5, 44.47) * mm});
            skArc(sketch, "E14.1.62.0", {"start": v(57.16, 52.38) * mm, "mid": v(57.41, 52.93) * mm, "end": v(57.2, 53.5) * mm});
            skLineSegment(sketch, "E14.4.62.0", {"start": v(56.18, 51.48) * mm, "end": v(57.16, 52.38) * mm});
            skArc(sketch, "E14.7.62.0", {"start": v(56.18, 51.48) * mm, "mid": v(55.8, 50.66) * mm, "end": v(55.45, 49.82) * mm});
            skArc(sketch, "E14.11.62.0", {"start": v(55.45, 49.82) * mm, "mid": v(55.41, 49.38) * mm, "end": v(55.62, 48.99) * mm});
            skLineSegment(sketch, "E14.15.62.0", {"start": v(55.62, 48.99) * mm, "end": v(55.83, 48.75) * mm});
            skArc(sketch, "E14.18.62.0", {"start": v(55.83, 48.75) * mm, "mid": v(56.19, 48.5) * mm, "end": v(56.63, 48.47) * mm});
            skArc(sketch, "E14.22.62.0", {"start": v(58.37, 48.98) * mm, "mid": v(57.5, 48.7) * mm, "end": v(56.63, 48.47) * mm});
            skLineSegment(sketch, "E14.26.62.0", {"start": v(58.37, 48.98) * mm, "end": v(59.39, 49.83) * mm});
            skArc(sketch, "E14.29.62.0", {"start": v(60.5, 49.73) * mm, "mid": v(59.97, 50.01) * mm, "end": v(59.39, 49.83) * mm});
            skArc(sketch, "E14.1.63.0", {"start": v(52.38, 57.16) * mm, "mid": v(52.58, 57.73) * mm, "end": v(52.32, 58.28) * mm});
            skLineSegment(sketch, "E14.4.63.0", {"start": v(51.48, 56.18) * mm, "end": v(52.38, 57.16) * mm});
            skArc(sketch, "E14.7.63.0", {"start": v(51.48, 56.18) * mm, "mid": v(51.17, 55.33) * mm, "end": v(50.9, 54.46) * mm});
            skArc(sketch, "E14.11.63.0", {"start": v(50.9, 54.46) * mm, "mid": v(50.9, 54.02) * mm, "end": v(51.13, 53.65) * mm});
            skLineSegment(sketch, "E14.15.63.0", {"start": v(51.13, 53.65) * mm, "end": v(51.37, 53.43) * mm});
            skArc(sketch, "E14.18.63.0", {"start": v(51.37, 53.43) * mm, "mid": v(51.75, 53.2) * mm, "end": v(52.19, 53.22) * mm});
            skArc(sketch, "E14.22.63.0", {"start": v(53.88, 53.88) * mm, "mid": v(53.04, 53.53) * mm, "end": v(52.19, 53.22) * mm});
            skLineSegment(sketch, "E14.26.63.0", {"start": v(53.88, 53.88) * mm, "end": v(54.82, 54.82) * mm});
            skArc(sketch, "E14.29.63.0", {"start": v(55.94, 54.81) * mm, "mid": v(55.38, 55.05) * mm, "end": v(54.82, 54.82) * mm});
            skArc(sketch, "E14.1.64.0", {"start": v(47.2, 61.5) * mm, "mid": v(47.35, 62.1) * mm, "end": v(47.04, 62.61) * mm});
            skLineSegment(sketch, "E14.4.64.0", {"start": v(46.39, 60.45) * mm, "end": v(47.2, 61.5) * mm});
            skArc(sketch, "E14.7.64.0", {"start": v(46.39, 60.45) * mm, "mid": v(46.15, 59.58) * mm, "end": v(45.96, 58.69) * mm});
            skArc(sketch, "E14.11.64.0", {"start": v(45.96, 58.69) * mm, "mid": v(46, 58.25) * mm, "end": v(46.26, 57.9) * mm});
            skLineSegment(sketch, "E14.15.64.0", {"start": v(46.26, 57.9) * mm, "end": v(46.52, 57.7) * mm});
            skArc(sketch, "E14.18.64.0", {"start": v(46.52, 57.7) * mm, "mid": v(46.91, 57.51) * mm, "end": v(47.35, 57.57) * mm});
            skArc(sketch, "E14.22.64.0", {"start": v(48.98, 58.37) * mm, "mid": v(48.17, 57.95) * mm, "end": v(47.35, 57.57) * mm});
            skLineSegment(sketch, "E14.26.64.0", {"start": v(48.98, 58.37) * mm, "end": v(49.83, 59.39) * mm});
            skArc(sketch, "E14.29.64.0", {"start": v(50.95, 59.48) * mm, "mid": v(50.37, 59.67) * mm, "end": v(49.83, 59.39) * mm});
            skArc(sketch, "E14.1.65.0", {"start": v(41.65, 65.38) * mm, "mid": v(41.76, 65.98) * mm, "end": v(41.4, 66.48) * mm});
            skLineSegment(sketch, "E14.4.65.0", {"start": v(40.94, 64.27) * mm, "end": v(41.65, 65.38) * mm});
            skArc(sketch, "E14.7.65.0", {"start": v(40.94, 64.27) * mm, "mid": v(40.78, 63.37) * mm, "end": v(40.67, 62.47) * mm});
            skArc(sketch, "E14.11.65.0", {"start": v(40.67, 62.47) * mm, "mid": v(40.74, 62.04) * mm, "end": v(41.04, 61.71) * mm});
            skLineSegment(sketch, "E14.15.65.0", {"start": v(41.04, 61.71) * mm, "end": v(41.31, 61.53) * mm});
            skArc(sketch, "E14.18.65.0", {"start": v(41.31, 61.53) * mm, "mid": v(41.72, 61.38) * mm, "end": v(42.15, 61.48) * mm});
            skArc(sketch, "E14.22.65.0", {"start": v(43.7, 62.42) * mm, "mid": v(42.94, 61.93) * mm, "end": v(42.15, 61.48) * mm});
            skLineSegment(sketch, "E14.26.65.0", {"start": v(43.7, 62.42) * mm, "end": v(44.47, 63.5) * mm});
            skArc(sketch, "E14.29.65.0", {"start": v(45.57, 63.7) * mm, "mid": v(44.98, 63.83) * mm, "end": v(44.47, 63.5) * mm});
            skArc(sketch, "E14.1.66.0", {"start": v(35.8, 68.77) * mm, "mid": v(35.85, 69.37) * mm, "end": v(35.46, 69.83) * mm});
            skLineSegment(sketch, "E14.4.66.0", {"start": v(35.19, 67.6) * mm, "end": v(35.8, 68.77) * mm});
            skArc(sketch, "E14.7.66.0", {"start": v(35.19, 67.6) * mm, "mid": v(35.1, 66.68) * mm, "end": v(35.07, 65.78) * mm});
            skArc(sketch, "E14.11.66.0", {"start": v(35.07, 65.78) * mm, "mid": v(35.18, 65.35) * mm, "end": v(35.5, 65.06) * mm});
            skLineSegment(sketch, "E14.15.66.0", {"start": v(35.5, 65.06) * mm, "end": v(35.8, 64.9) * mm});
            skArc(sketch, "E14.18.66.0", {"start": v(35.8, 64.9) * mm, "mid": v(36.21, 64.79) * mm, "end": v(36.63, 64.92) * mm});
            skArc(sketch, "E14.22.66.0", {"start": v(38.1, 66) * mm, "mid": v(37.38, 65.44) * mm, "end": v(36.63, 64.92) * mm});
            skLineSegment(sketch, "E14.26.66.0", {"start": v(38.1, 66) * mm, "end": v(38.76, 67.14) * mm});
            skArc(sketch, "E14.29.66.0", {"start": v(39.85, 67.42) * mm, "mid": v(39.24, 67.5) * mm, "end": v(38.76, 67.14) * mm});
            skArc(sketch, "E14.1.67.0", {"start": v(29.67, 71.62) * mm, "mid": v(29.67, 72.23) * mm, "end": v(29.23, 72.66) * mm});
            skLineSegment(sketch, "E14.4.67.0", {"start": v(29.16, 70.4) * mm, "end": v(29.67, 71.62) * mm});
            skArc(sketch, "E14.7.67.0", {"start": v(29.16, 70.4) * mm, "mid": v(29.16, 69.5) * mm, "end": v(29.2, 68.58) * mm});
            skArc(sketch, "E14.11.67.0", {"start": v(29.2, 68.58) * mm, "mid": v(29.35, 68.17) * mm, "end": v(29.7, 67.9) * mm});
            skLineSegment(sketch, "E14.15.67.0", {"start": v(29.7, 67.9) * mm, "end": v(30, 67.77) * mm});
            skArc(sketch, "E14.18.67.0", {"start": v(30, 67.77) * mm, "mid": v(30.43, 67.7) * mm, "end": v(30.84, 67.86) * mm});
            skArc(sketch, "E14.22.67.0", {"start": v(32.2, 69.06) * mm, "mid": v(31.53, 68.45) * mm, "end": v(30.84, 67.86) * mm});
            skLineSegment(sketch, "E14.26.67.0", {"start": v(32.2, 69.06) * mm, "end": v(32.76, 70.26) * mm});
            skArc(sketch, "E14.29.67.0", {"start": v(33.82, 70.64) * mm, "mid": v(33.21, 70.67) * mm, "end": v(32.76, 70.26) * mm});
            skArc(sketch, "E14.1.68.0", {"start": v(23.31, 73.94) * mm, "mid": v(23.26, 74.54) * mm, "end": v(22.8, 74.93) * mm});
            skLineSegment(sketch, "E14.4.68.0", {"start": v(22.91, 72.67) * mm, "end": v(23.31, 73.94) * mm});
            skArc(sketch, "E14.7.68.0", {"start": v(22.91, 72.67) * mm, "mid": v(23, 71.77) * mm, "end": v(23.11, 70.87) * mm});
            skArc(sketch, "E14.11.68.0", {"start": v(23.11, 70.87) * mm, "mid": v(23.3, 70.47) * mm, "end": v(23.67, 70.23) * mm});
            skLineSegment(sketch, "E14.15.68.0", {"start": v(23.67, 70.23) * mm, "end": v(23.98, 70.13) * mm});
            skArc(sketch, "E14.18.68.0", {"start": v(23.98, 70.13) * mm, "mid": v(24.41, 70.1) * mm, "end": v(24.8, 70.3) * mm});
            skArc(sketch, "E14.22.68.0", {"start": v(26.06, 71.6) * mm, "mid": v(25.45, 70.93) * mm, "end": v(24.8, 70.3) * mm});
            skLineSegment(sketch, "E14.26.68.0", {"start": v(26.06, 71.6) * mm, "end": v(26.52, 72.85) * mm});
            skArc(sketch, "E14.29.68.0", {"start": v(27.53, 73.32) * mm, "mid": v(26.93, 73.3) * mm, "end": v(26.52, 72.85) * mm});
            skArc(sketch, "E14.1.69.0", {"start": v(16.78, 75.69) * mm, "mid": v(16.67, 76.28) * mm, "end": v(16.17, 76.63) * mm});
            skLineSegment(sketch, "E14.4.69.0", {"start": v(16.5, 74.4) * mm, "end": v(16.78, 75.69) * mm});
            skArc(sketch, "E14.7.69.0", {"start": v(16.5, 74.4) * mm, "mid": v(16.65, 73.5) * mm, "end": v(16.85, 72.61) * mm});
            skArc(sketch, "E14.11.69.0", {"start": v(16.85, 72.61) * mm, "mid": v(17.07, 72.23) * mm, "end": v(17.46, 72.03) * mm});
            skLineSegment(sketch, "E14.15.69.0", {"start": v(17.46, 72.03) * mm, "end": v(17.77, 71.95) * mm});
            skArc(sketch, "E14.18.69.0", {"start": v(17.77, 71.95) * mm, "mid": v(18.21, 71.95) * mm, "end": v(18.58, 72.19) * mm});
            skArc(sketch, "E14.22.69.0", {"start": v(19.72, 73.6) * mm, "mid": v(19.17, 72.88) * mm, "end": v(18.58, 72.19) * mm});
            skLineSegment(sketch, "E14.26.69.0", {"start": v(19.72, 73.6) * mm, "end": v(20.07, 74.88) * mm});
            skArc(sketch, "E14.29.69.0", {"start": v(21.04, 75.44) * mm, "mid": v(20.44, 75.36) * mm, "end": v(20.07, 74.88) * mm});
            skArc(sketch, "E14.1.70.0", {"start": v(10.12, 76.86) * mm, "mid": v(9.96, 77.45) * mm, "end": v(9.43, 77.75) * mm});
            skLineSegment(sketch, "E14.4.70.0", {"start": v(9.95, 75.55) * mm, "end": v(10.12, 76.86) * mm});
            skArc(sketch, "E14.7.70.0", {"start": v(9.95, 75.55) * mm, "mid": v(10.18, 74.67) * mm, "end": v(10.46, 73.8) * mm});
            skArc(sketch, "E14.11.70.0", {"start": v(10.46, 73.8) * mm, "mid": v(10.7, 73.44) * mm, "end": v(11.11, 73.28) * mm});
            skLineSegment(sketch, "E14.15.70.0", {"start": v(11.11, 73.28) * mm, "end": v(11.43, 73.23) * mm});
            skArc(sketch, "E14.18.70.0", {"start": v(11.43, 73.23) * mm, "mid": v(11.87, 73.26) * mm, "end": v(12.22, 73.53) * mm});
            skArc(sketch, "E14.22.70.0", {"start": v(13.23, 75.04) * mm, "mid": v(12.74, 74.27) * mm, "end": v(12.22, 73.53) * mm});
            skLineSegment(sketch, "E14.26.70.0", {"start": v(13.23, 75.04) * mm, "end": v(13.46, 76.35) * mm});
            skArc(sketch, "E14.29.70.0", {"start": v(14.38, 76.98) * mm, "mid": v(13.79, 76.86) * mm, "end": v(13.46, 76.35) * mm});
            skArc(sketch, "E14.1.71.0", {"start": v(3.38, 77.45) * mm, "mid": v(3.17, 78.02) * mm, "end": v(2.62, 78.27) * mm});
            skLineSegment(sketch, "E14.4.71.0", {"start": v(3.32, 76.13) * mm, "end": v(3.38, 77.45) * mm});
            skArc(sketch, "E14.7.71.0", {"start": v(3.32, 76.13) * mm, "mid": v(3.63, 75.27) * mm, "end": v(3.98, 74.43) * mm});
            skArc(sketch, "E14.11.71.0", {"start": v(3.98, 74.43) * mm, "mid": v(4.27, 74.1) * mm, "end": v(4.69, 73.97) * mm});
            skLineSegment(sketch, "E14.15.71.0", {"start": v(4.69, 73.97) * mm, "end": v(5, 73.94) * mm});
            skArc(sketch, "E14.18.71.0", {"start": v(5, 73.94) * mm, "mid": v(5.44, 74.02) * mm, "end": v(5.77, 74.32) * mm});
            skArc(sketch, "E14.22.71.0", {"start": v(6.64, 75.91) * mm, "mid": v(6.22, 75.1) * mm, "end": v(5.77, 74.32) * mm});
            skLineSegment(sketch, "E14.26.71.0", {"start": v(6.64, 75.91) * mm, "end": v(6.76, 77.23) * mm});
            skArc(sketch, "E14.29.71.0", {"start": v(7.62, 77.95) * mm, "mid": v(7.04, 77.77) * mm, "end": v(6.76, 77.23) * mm});
            skArc(sketch, "E15.trimOffspring", {"start": v(2.62, 78.27) * mm, "mid": v(1.7, 78.3) * mm, "end": v(0.8, 78.31) * mm});
            skArc(sketch, "E16.trimOffspring", {"start": v(9.43, 77.75) * mm, "mid": v(8.53, 77.85) * mm, "end": v(7.62, 77.95) * mm});
            skArc(sketch, "E17.trimOffspring", {"start": v(-17.73, 76.28) * mm, "mid": v(-18.61, 76.07) * mm, "end": v(-19.5, 75.85) * mm});
            skArc(sketch, "E18.trimOffspring", {"start": v(-11.01, 77.54) * mm, "mid": v(-11.91, 77.4) * mm, "end": v(-12.82, 77.26) * mm});
            skArc(sketch, "E19.trimOffspring", {"start": v(16.17, 76.63) * mm, "mid": v(15.28, 76.81) * mm, "end": v(14.38, 76.98) * mm});
            skArc(sketch, "E20.trimOffspring", {"start": v(22.8, 74.93) * mm, "mid": v(21.92, 75.19) * mm, "end": v(21.04, 75.44) * mm});
            skArc(sketch, "E21.trimOffspring", {"start": v(29.23, 72.66) * mm, "mid": v(28.38, 73) * mm, "end": v(27.53, 73.32) * mm});
            skArc(sketch, "E22.trimOffspring", {"start": v(35.46, 69.83) * mm, "mid": v(34.64, 70.24) * mm, "end": v(33.82, 70.64) * mm});
            skArc(sketch, "E23.trimOffspring", {"start": v(41.4, 66.48) * mm, "mid": v(40.63, 66.95) * mm, "end": v(39.85, 67.42) * mm});
            skArc(sketch, "E24.trimOffspring", {"start": v(47.04, 62.61) * mm, "mid": v(46.3, 63.16) * mm, "end": v(45.57, 63.7) * mm});
            skArc(sketch, "E25.trimOffspring", {"start": v(-24.3, 74.45) * mm, "mid": v(-25.17, 74.16) * mm, "end": v(-26.04, 73.86) * mm});
            skArc(sketch, "E26.trimOffspring", {"start": v(-30.7, 72.05) * mm, "mid": v(-31.54, 71.68) * mm, "end": v(-32.38, 71.31) * mm});
            skArc(sketch, "E27.trimOffspring", {"start": v(-36.87, 69.1) * mm, "mid": v(-37.67, 68.66) * mm, "end": v(-38.47, 68.22) * mm});
            skArc(sketch, "E28.trimOffspring", {"start": v(-42.75, 65.62) * mm, "mid": v(-43.51, 65.12) * mm, "end": v(-44.27, 64.6) * mm});
            skArc(sketch, "E29.trimOffspring", {"start": v(-48.3, 61.65) * mm, "mid": v(-49.02, 61.08) * mm, "end": v(-49.73, 60.5) * mm});
            skArc(sketch, "E30.trimOffspring", {"start": v(-53.5, 57.2) * mm, "mid": v(-54.16, 56.57) * mm, "end": v(-54.81, 55.94) * mm});
            skArc(sketch, "E31.trimOffspring", {"start": v(52.32, 58.28) * mm, "mid": v(51.64, 58.88) * mm, "end": v(50.95, 59.48) * mm});
            skArc(sketch, "E32.trimOffspring", {"start": v(57.2, 53.5) * mm, "mid": v(56.57, 54.16) * mm, "end": v(55.94, 54.81) * mm});
            skArc(sketch, "E33.trimOffspring", {"start": v(61.65, 48.3) * mm, "mid": v(61.08, 49.02) * mm, "end": v(60.5, 49.73) * mm});
            skArc(sketch, "E34.trimOffspring", {"start": v(65.62, 42.75) * mm, "mid": v(65.12, 43.51) * mm, "end": v(64.6, 44.27) * mm});
            skArc(sketch, "E35.trimOffspring", {"start": v(69.1, 36.87) * mm, "mid": v(68.66, 37.67) * mm, "end": v(68.22, 38.47) * mm});
            skArc(sketch, "E36.trimOffspring", {"start": v(-58.28, 52.32) * mm, "mid": v(-58.88, 51.64) * mm, "end": v(-59.48, 50.95) * mm});
            skArc(sketch, "E37.trimOffspring", {"start": v(-62.61, 47.04) * mm, "mid": v(-63.16, 46.3) * mm, "end": v(-63.7, 45.57) * mm});
            skArc(sketch, "E38.trimOffspring", {"start": v(-66.48, 41.4) * mm, "mid": v(-66.95, 40.63) * mm, "end": v(-67.42, 39.85) * mm});
            skArc(sketch, "E39.trimOffspring", {"start": v(72.05, 30.7) * mm, "mid": v(71.68, 31.54) * mm, "end": v(71.31, 32.38) * mm});
            skArc(sketch, "E40.trimOffspring", {"start": v(74.45, 24.3) * mm, "mid": v(74.16, 25.17) * mm, "end": v(73.86, 26.04) * mm});
            skArc(sketch, "E41.trimOffspring", {"start": v(76.28, 17.73) * mm, "mid": v(76.07, 18.61) * mm, "end": v(75.85, 19.5) * mm});
            skArc(sketch, "E42.trimOffspring", {"start": v(-69.83, 35.46) * mm, "mid": v(-70.24, 34.64) * mm, "end": v(-70.64, 33.82) * mm});
            skArc(sketch, "E43.trimOffspring", {"start": v(77.54, 11.01) * mm, "mid": v(77.4, 11.91) * mm, "end": v(77.26, 12.82) * mm});
            skArc(sketch, "E44.trimOffspring", {"start": v(78.2, 4.21) * mm, "mid": v(78.15, 5.12) * mm, "end": v(78.08, 6.03) * mm});
            skArc(sketch, "E45.trimOffspring", {"start": v(78.27, -2.62) * mm, "mid": v(78.3, -1.7) * mm, "end": v(78.31, -0.8) * mm});
            skArc(sketch, "E46.trimOffspring", {"start": v(77.75, -9.43) * mm, "mid": v(77.85, -8.53) * mm, "end": v(77.95, -7.62) * mm});
            skArc(sketch, "E47.trimOffspring", {"start": v(76.63, -16.17) * mm, "mid": v(76.81, -15.28) * mm, "end": v(76.98, -14.38) * mm});
            skArc(sketch, "E48.trimOffspring", {"start": v(74.93, -22.8) * mm, "mid": v(75.19, -21.92) * mm, "end": v(75.44, -21.04) * mm});
            skArc(sketch, "E49.trimOffspring", {"start": v(72.66, -29.23) * mm, "mid": v(73, -28.38) * mm, "end": v(73.32, -27.53) * mm});
            skArc(sketch, "E50.trimOffspring", {"start": v(69.83, -35.46) * mm, "mid": v(70.24, -34.64) * mm, "end": v(70.64, -33.82) * mm});
            skArc(sketch, "E51.trimOffspring", {"start": v(66.48, -41.4) * mm, "mid": v(66.95, -40.63) * mm, "end": v(67.42, -39.85) * mm});
            skArc(sketch, "E52.trimOffspring", {"start": v(62.61, -47.04) * mm, "mid": v(63.16, -46.3) * mm, "end": v(63.7, -45.57) * mm});
            skArc(sketch, "E53.trimOffspring", {"start": v(58.28, -52.32) * mm, "mid": v(58.88, -51.64) * mm, "end": v(59.48, -50.95) * mm});
            skArc(sketch, "E54.trimOffspring", {"start": v(53.5, -57.2) * mm, "mid": v(54.16, -56.57) * mm, "end": v(54.81, -55.94) * mm});
            skArc(sketch, "E55.trimOffspring", {"start": v(48.3, -61.65) * mm, "mid": v(49.02, -61.08) * mm, "end": v(49.73, -60.5) * mm});
            skArc(sketch, "E56.trimOffspring", {"start": v(42.75, -65.62) * mm, "mid": v(43.51, -65.12) * mm, "end": v(44.27, -64.6) * mm});
            skArc(sketch, "E57.trimOffspring", {"start": v(36.87, -69.1) * mm, "mid": v(37.67, -68.66) * mm, "end": v(38.47, -68.22) * mm});
            skArc(sketch, "E58.trimOffspring", {"start": v(30.7, -72.05) * mm, "mid": v(31.54, -71.68) * mm, "end": v(32.38, -71.31) * mm});
            skArc(sketch, "E59.trimOffspring", {"start": v(24.3, -74.45) * mm, "mid": v(25.17, -74.16) * mm, "end": v(26.04, -73.86) * mm});
            skArc(sketch, "E60.trimOffspring", {"start": v(17.73, -76.28) * mm, "mid": v(18.61, -76.07) * mm, "end": v(19.5, -75.85) * mm});
            skArc(sketch, "E61.trimOffspring", {"start": v(11.01, -77.54) * mm, "mid": v(11.91, -77.4) * mm, "end": v(12.82, -77.26) * mm});
            skArc(sketch, "E62.trimOffspring", {"start": v(4.21, -78.2) * mm, "mid": v(5.12, -78.15) * mm, "end": v(6.03, -78.08) * mm});
            skArc(sketch, "E63.trimOffspring", {"start": v(-2.62, -78.27) * mm, "mid": v(-1.7, -78.3) * mm, "end": v(-0.8, -78.31) * mm});
            skArc(sketch, "E64.trimOffspring", {"start": v(-9.43, -77.75) * mm, "mid": v(-8.53, -77.85) * mm, "end": v(-7.62, -77.95) * mm});
            skArc(sketch, "E65.trimOffspring", {"start": v(-16.17, -76.63) * mm, "mid": v(-15.28, -76.81) * mm, "end": v(-14.38, -76.98) * mm});
            skArc(sketch, "E66.trimOffspring", {"start": v(-22.8, -74.93) * mm, "mid": v(-21.92, -75.19) * mm, "end": v(-21.04, -75.44) * mm});
            skArc(sketch, "E67.trimOffspring", {"start": v(-29.23, -72.66) * mm, "mid": v(-28.38, -73) * mm, "end": v(-27.53, -73.32) * mm});
            skArc(sketch, "E68.trimOffspring", {"start": v(-35.46, -69.83) * mm, "mid": v(-34.64, -70.24) * mm, "end": v(-33.82, -70.64) * mm});
            skArc(sketch, "E69.trimOffspring", {"start": v(-41.4, -66.48) * mm, "mid": v(-40.63, -66.95) * mm, "end": v(-39.85, -67.42) * mm});
            skArc(sketch, "E70.trimOffspring", {"start": v(-47.04, -62.61) * mm, "mid": v(-46.3, -63.16) * mm, "end": v(-45.57, -63.7) * mm});
            skArc(sketch, "E71.trimOffspring", {"start": v(-52.32, -58.28) * mm, "mid": v(-51.64, -58.88) * mm, "end": v(-50.95, -59.48) * mm});
            skArc(sketch, "E72.trimOffspring", {"start": v(-57.2, -53.5) * mm, "mid": v(-56.57, -54.16) * mm, "end": v(-55.94, -54.81) * mm});
            skArc(sketch, "E73.trimOffspring", {"start": v(-61.65, -48.3) * mm, "mid": v(-61.08, -49.02) * mm, "end": v(-60.5, -49.73) * mm});
            skArc(sketch, "E74.trimOffspring", {"start": v(-65.62, -42.75) * mm, "mid": v(-65.12, -43.51) * mm, "end": v(-64.6, -44.27) * mm});
            skArc(sketch, "E75.trimOffspring", {"start": v(-69.1, -36.87) * mm, "mid": v(-68.66, -37.67) * mm, "end": v(-68.22, -38.47) * mm});
            skArc(sketch, "E76.trimOffspring", {"start": v(-72.05, -30.7) * mm, "mid": v(-71.68, -31.54) * mm, "end": v(-71.31, -32.38) * mm});
            skArc(sketch, "E77.trimOffspring", {"start": v(-74.45, -24.3) * mm, "mid": v(-74.16, -25.17) * mm, "end": v(-73.86, -26.04) * mm});
            skArc(sketch, "E78.trimOffspring", {"start": v(-76.28, -17.73) * mm, "mid": v(-76.07, -18.61) * mm, "end": v(-75.85, -19.5) * mm});
            skArc(sketch, "E79.trimOffspring", {"start": v(-77.54, -11.01) * mm, "mid": v(-77.4, -11.91) * mm, "end": v(-77.26, -12.82) * mm});
            skArc(sketch, "E80.trimOffspring", {"start": v(-78.2, -4.21) * mm, "mid": v(-78.15, -5.12) * mm, "end": v(-78.08, -6.03) * mm});
            skArc(sketch, "E81.trimOffspring", {"start": v(-78.27, 2.62) * mm, "mid": v(-78.3, 1.7) * mm, "end": v(-78.31, 0.8) * mm});
            skArc(sketch, "E82.trimOffspring", {"start": v(-77.75, 9.43) * mm, "mid": v(-77.85, 8.53) * mm, "end": v(-77.95, 7.62) * mm});
            skArc(sketch, "E83.trimOffspring", {"start": v(-76.63, 16.17) * mm, "mid": v(-76.81, 15.28) * mm, "end": v(-76.98, 14.38) * mm});
            skArc(sketch, "E84.trimOffspring", {"start": v(-74.93, 22.8) * mm, "mid": v(-75.19, 21.92) * mm, "end": v(-75.44, 21.04) * mm});
            skArc(sketch, "E85.trimOffspring", {"start": v(-72.66, 29.23) * mm, "mid": v(-73, 28.38) * mm, "end": v(-73.32, 27.53) * mm});
            skSolve(sketch);
        }
        {
            var Q0;
            Q0=makeQuery(id+"F0.imprint","IMPRINT",FACE,{"disambiguationData":[TD([[makeQuery(id+"F0.imprint","IMPRINT",EDGE,{"derivedFrom":sQuery(id+"F0.wireOp",EDGE,"E0")}),1.0]])]});
            extrude(context, id + "F1", {"entities" : qUnion([Q0]), "depth" : 6.35 * mm});
        }
        {
            var Q0;
            Q0=makeQuery(id+"F0.imprint","IMPRINT",FACE,{"disambiguationData":[TD([[makeQuery(id+"F0.imprint","IMPRINT",EDGE,{"derivedFrom":sQuery(id+"F0.wireOp",EDGE,"E0")}),-1.0]])]});
            extrude(context, id + "F2", {"entities" : qUnion([Q0]), "operationType" : NewBodyOperationType.ADD, "depth" : 19.05 * mm});
        }
        {
            var Q0;
            Q0=makeQuery(id+"F1.opExtrude","CAP_FACE",FACE,{"disambiguationData":[OSD([sQuery(id+"F0.wireOp",EDGE,"E0"),sQuery(id+"F0.wireOp",EDGE,"E1.MirrorCS"),sQuery(id+"F0.wireOp",EDGE,"E2.MirrorCS"),sQuery(id+"F0.wireOp",EDGE,"E3.MirrorCS"),sQuery(id+"F0.wireOp",EDGE,"E4.MirrorCS"),sQuery(id+"F0.wireOp",EDGE,"E5.filletArc"),sQuery(id+"F0.wireOp",EDGE,"E6.filletArc"),sQuery(id+"F0.wireOp",EDGE,"E7"),sQuery(id+"F0.wireOp",EDGE,"E11.filletArc"),sQuery(id+"F0.wireOp",EDGE,"E12.filletArc"),sQuery(id+"F0.wireOp",EDGE,"E13.1.0"),sQuery(id+"F0.wireOp",EDGE,"E13.1.1"),sQuery(id+"F0.wireOp",EDGE,"E13.1.2"),sQuery(id+"F0.wireOp",EDGE,"E13.1.3"),sQuery(id+"F0.wireOp",EDGE,"E13.1.4"),sQuery(id+"F0.wireOp",EDGE,"E13.1.5"),sQuery(id+"F0.wireOp",EDGE,"E13.1.6"),sQuery(id+"F0.wireOp",EDGE,"E13.1.7"),sQuery(id+"F0.wireOp",EDGE,"E13.1.8"),sQuery(id+"F0.wireOp",EDGE,"E13.2.0"),sQuery(id+"F0.wireOp",EDGE,"E13.2.1"),sQuery(id+"F0.wireOp",EDGE,"E13.2.2"),sQuery(id+"F0.wireOp",EDGE,"E13.2.3"),sQuery(id+"F0.wireOp",EDGE,"E13.2.4"),sQuery(id+"F0.wireOp",EDGE,"E13.2.5"),sQuery(id+"F0.wireOp",EDGE,"E13.2.6"),sQuery(id+"F0.wireOp",EDGE,"E13.2.7"),sQuery(id+"F0.wireOp",EDGE,"E13.2.8"),sQuery(id+"F0.wireOp",EDGE,"E14.1.3.0"),sQuery(id+"F0.wireOp",EDGE,"E14.4.3.0"),sQuery(id+"F0.wireOp",EDGE,"E14.7.3.0"),sQuery(id+"F0.wireOp",EDGE,"E14.11.3.0"),sQuery(id+"F0.wireOp",EDGE,"E14.15.3.0"),sQuery(id+"F0.wireOp",EDGE,"E14.18.3.0"),sQuery(id+"F0.wireOp",EDGE,"E14.22.3.0"),sQuery(id+"F0.wireOp",EDGE,"E14.26.3.0"),sQuery(id+"F0.wireOp",EDGE,"E14.29.3.0"),sQuery(id+"F0.wireOp",EDGE,"E14.1.4.0"),sQuery(id+"F0.wireOp",EDGE,"E14.4.4.0"),sQuery(id+"F0.wireOp",EDGE,"E14.7.4.0"),sQuery(id+"F0.wireOp",EDGE,"E14.11.4.0"),sQuery(id+"F0.wireOp",EDGE,"E14.15.4.0"),sQuery(id+"F0.wireOp",EDGE,"E14.18.4.0"),sQuery(id+"F0.wireOp",EDGE,"E14.22.4.0"),sQuery(id+"F0.wireOp",EDGE,"E14.26.4.0"),sQuery(id+"F0.wireOp",EDGE,"E14.29.4.0"),sQuery(id+"F0.wireOp",EDGE,"E14.1.5.0"),sQuery(id+"F0.wireOp",EDGE,"E14.4.5.0"),sQuery(id+"F0.wireOp",EDGE,"E14.7.5.0"),sQuery(id+"F0.wireOp",EDGE,"E14.11.5.0"),sQuery(id+"F0.wireOp",EDGE,"E14.15.5.0"),sQuery(id+"F0.wireOp",EDGE,"E14.18.5.0"),sQuery(id+"F0.wireOp",EDGE,"E14.22.5.0"),sQuery(id+"F0.wireOp",EDGE,"E14.26.5.0"),sQuery(id+"F0.wireOp",EDGE,"E14.29.5.0"),sQuery(id+"F0.wireOp",EDGE,"E14.1.6.0"),sQuery(id+"F0.wireOp",EDGE,"E14.4.6.0"),sQuery(id+"F0.wireOp",EDGE,"E14.7.6.0"),sQuery(id+"F0.wireOp",EDGE,"E14.11.6.0"),sQuery(id+"F0.wireOp",EDGE,"E14.15.6.0"),sQuery(id+"F0.wireOp",EDGE,"E14.18.6.0"),sQuery(id+"F0.wireOp",EDGE,"E14.22.6.0"),sQuery(id+"F0.wireOp",EDGE,"E14.26.6.0"),sQuery(id+"F0.wireOp",EDGE,"E14.29.6.0"),sQuery(id+"F0.wireOp",EDGE,"E14.1.7.0"),sQuery(id+"F0.wireOp",EDGE,"E14.4.7.0"),sQuery(id+"F0.wireOp",EDGE,"E14.7.7.0"),sQuery(id+"F0.wireOp",EDGE,"E14.11.7.0"),sQuery(id+"F0.wireOp",EDGE,"E14.15.7.0"),sQuery(id+"F0.wireOp",EDGE,"E14.18.7.0"),sQuery(id+"F0.wireOp",EDGE,"E14.22.7.0"),sQuery(id+"F0.wireOp",EDGE,"E14.26.7.0"),sQuery(id+"F0.wireOp",EDGE,"E14.29.7.0"),sQuery(id+"F0.wireOp",EDGE,"E14.1.8.0"),sQuery(id+"F0.wireOp",EDGE,"E14.4.8.0"),sQuery(id+"F0.wireOp",EDGE,"E14.7.8.0"),sQuery(id+"F0.wireOp",EDGE,"E14.11.8.0"),sQuery(id+"F0.wireOp",EDGE,"E14.15.8.0"),sQuery(id+"F0.wireOp",EDGE,"E14.18.8.0"),sQuery(id+"F0.wireOp",EDGE,"E14.22.8.0"),sQuery(id+"F0.wireOp",EDGE,"E14.26.8.0"),sQuery(id+"F0.wireOp",EDGE,"E14.29.8.0"),sQuery(id+"F0.wireOp",EDGE,"E14.1.9.0"),sQuery(id+"F0.wireOp",EDGE,"E14.4.9.0"),sQuery(id+"F0.wireOp",EDGE,"E14.7.9.0"),sQuery(id+"F0.wireOp",EDGE,"E14.11.9.0"),sQuery(id+"F0.wireOp",EDGE,"E14.15.9.0"),sQuery(id+"F0.wireOp",EDGE,"E14.18.9.0"),sQuery(id+"F0.wireOp",EDGE,"E14.22.9.0"),sQuery(id+"F0.wireOp",EDGE,"E14.26.9.0"),sQuery(id+"F0.wireOp",EDGE,"E14.29.9.0"),sQuery(id+"F0.wireOp",EDGE,"E14.1.10.0"),sQuery(id+"F0.wireOp",EDGE,"E14.4.10.0"),sQuery(id+"F0.wireOp",EDGE,"E14.7.10.0"),sQuery(id+"F0.wireOp",EDGE,"E14.11.10.0"),sQuery(id+"F0.wireOp",EDGE,"E14.15.10.0"),sQuery(id+"F0.wireOp",EDGE,"E14.18.10.0"),sQuery(id+"F0.wireOp",EDGE,"E14.22.10.0"),sQuery(id+"F0.wireOp",EDGE,"E14.26.10.0"),sQuery(id+"F0.wireOp",EDGE,"E14.29.10.0"),sQuery(id+"F0.wireOp",EDGE,"E14.1.11.0"),sQuery(id+"F0.wireOp",EDGE,"E14.4.11.0"),sQuery(id+"F0.wireOp",EDGE,"E14.7.11.0"),sQuery(id+"F0.wireOp",EDGE,"E14.11.11.0"),sQuery(id+"F0.wireOp",EDGE,"E14.15.11.0"),sQuery(id+"F0.wireOp",EDGE,"E14.18.11.0"),sQuery(id+"F0.wireOp",EDGE,"E14.22.11.0"),sQuery(id+"F0.wireOp",EDGE,"E14.26.11.0"),sQuery(id+"F0.wireOp",EDGE,"E14.29.11.0"),sQuery(id+"F0.wireOp",EDGE,"E14.1.12.0"),sQuery(id+"F0.wireOp",EDGE,"E14.4.12.0"),sQuery(id+"F0.wireOp",EDGE,"E14.7.12.0"),sQuery(id+"F0.wireOp",EDGE,"E14.11.12.0"),sQuery(id+"F0.wireOp",EDGE,"E14.15.12.0"),sQuery(id+"F0.wireOp",EDGE,"E14.18.12.0"),sQuery(id+"F0.wireOp",EDGE,"E14.22.12.0"),sQuery(id+"F0.wireOp",EDGE,"E14.26.12.0"),sQuery(id+"F0.wireOp",EDGE,"E14.29.12.0"),sQuery(id+"F0.wireOp",EDGE,"E14.1.13.0"),sQuery(id+"F0.wireOp",EDGE,"E14.4.13.0"),sQuery(id+"F0.wireOp",EDGE,"E14.7.13.0"),sQuery(id+"F0.wireOp",EDGE,"E14.11.13.0"),sQuery(id+"F0.wireOp",EDGE,"E14.15.13.0"),sQuery(id+"F0.wireOp",EDGE,"E14.18.13.0"),sQuery(id+"F0.wireOp",EDGE,"E14.22.13.0"),sQuery(id+"F0.wireOp",EDGE,"E14.26.13.0"),sQuery(id+"F0.wireOp",EDGE,"E14.29.13.0"),sQuery(id+"F0.wireOp",EDGE,"E14.1.14.0"),sQuery(id+"F0.wireOp",EDGE,"E14.4.14.0"),sQuery(id+"F0.wireOp",EDGE,"E14.7.14.0"),sQuery(id+"F0.wireOp",EDGE,"E14.11.14.0"),sQuery(id+"F0.wireOp",EDGE,"E14.15.14.0"),sQuery(id+"F0.wireOp",EDGE,"E14.18.14.0"),sQuery(id+"F0.wireOp",EDGE,"E14.22.14.0"),sQuery(id+"F0.wireOp",EDGE,"E14.26.14.0"),sQuery(id+"F0.wireOp",EDGE,"E14.29.14.0"),sQuery(id+"F0.wireOp",EDGE,"E14.1.15.0"),sQuery(id+"F0.wireOp",EDGE,"E14.4.15.0"),sQuery(id+"F0.wireOp",EDGE,"E14.7.15.0"),sQuery(id+"F0.wireOp",EDGE,"E14.11.15.0"),sQuery(id+"F0.wireOp",EDGE,"E14.15.15.0"),sQuery(id+"F0.wireOp",EDGE,"E14.18.15.0"),sQuery(id+"F0.wireOp",EDGE,"E14.22.15.0"),sQuery(id+"F0.wireOp",EDGE,"E14.26.15.0"),sQuery(id+"F0.wireOp",EDGE,"E14.29.15.0"),sQuery(id+"F0.wireOp",EDGE,"E14.1.16.0"),sQuery(id+"F0.wireOp",EDGE,"E14.4.16.0"),sQuery(id+"F0.wireOp",EDGE,"E14.7.16.0"),sQuery(id+"F0.wireOp",EDGE,"E14.11.16.0"),sQuery(id+"F0.wireOp",EDGE,"E14.15.16.0"),sQuery(id+"F0.wireOp",EDGE,"E14.18.16.0"),sQuery(id+"F0.wireOp",EDGE,"E14.22.16.0"),sQuery(id+"F0.wireOp",EDGE,"E14.26.16.0"),sQuery(id+"F0.wireOp",EDGE,"E14.29.16.0"),sQuery(id+"F0.wireOp",EDGE,"E14.1.17.0"),sQuery(id+"F0.wireOp",EDGE,"E14.4.17.0"),sQuery(id+"F0.wireOp",EDGE,"E14.7.17.0"),sQuery(id+"F0.wireOp",EDGE,"E14.11.17.0"),sQuery(id+"F0.wireOp",EDGE,"E14.15.17.0"),sQuery(id+"F0.wireOp",EDGE,"E14.18.17.0"),sQuery(id+"F0.wireOp",EDGE,"E14.22.17.0"),sQuery(id+"F0.wireOp",EDGE,"E14.26.17.0"),sQuery(id+"F0.wireOp",EDGE,"E14.29.17.0"),sQuery(id+"F0.wireOp",EDGE,"E14.1.18.0"),sQuery(id+"F0.wireOp",EDGE,"E14.4.18.0"),sQuery(id+"F0.wireOp",EDGE,"E14.7.18.0"),sQuery(id+"F0.wireOp",EDGE,"E14.11.18.0"),sQuery(id+"F0.wireOp",EDGE,"E14.15.18.0"),sQuery(id+"F0.wireOp",EDGE,"E14.18.18.0"),sQuery(id+"F0.wireOp",EDGE,"E14.22.18.0"),sQuery(id+"F0.wireOp",EDGE,"E14.26.18.0"),sQuery(id+"F0.wireOp",EDGE,"E14.29.18.0"),sQuery(id+"F0.wireOp",EDGE,"E14.1.19.0"),sQuery(id+"F0.wireOp",EDGE,"E14.4.19.0"),sQuery(id+"F0.wireOp",EDGE,"E14.7.19.0"),sQuery(id+"F0.wireOp",EDGE,"E14.11.19.0"),sQuery(id+"F0.wireOp",EDGE,"E14.15.19.0"),sQuery(id+"F0.wireOp",EDGE,"E14.18.19.0"),sQuery(id+"F0.wireOp",EDGE,"E14.22.19.0"),sQuery(id+"F0.wireOp",EDGE,"E14.26.19.0"),sQuery(id+"F0.wireOp",EDGE,"E14.29.19.0"),sQuery(id+"F0.wireOp",EDGE,"E14.1.20.0"),sQuery(id+"F0.wireOp",EDGE,"E14.4.20.0"),sQuery(id+"F0.wireOp",EDGE,"E14.7.20.0"),sQuery(id+"F0.wireOp",EDGE,"E14.11.20.0"),sQuery(id+"F0.wireOp",EDGE,"E14.15.20.0"),sQuery(id+"F0.wireOp",EDGE,"E14.18.20.0"),sQuery(id+"F0.wireOp",EDGE,"E14.22.20.0"),sQuery(id+"F0.wireOp",EDGE,"E14.26.20.0"),sQuery(id+"F0.wireOp",EDGE,"E14.29.20.0"),sQuery(id+"F0.wireOp",EDGE,"E14.1.21.0"),sQuery(id+"F0.wireOp",EDGE,"E14.4.21.0"),sQuery(id+"F0.wireOp",EDGE,"E14.7.21.0"),sQuery(id+"F0.wireOp",EDGE,"E14.11.21.0"),sQuery(id+"F0.wireOp",EDGE,"E14.15.21.0"),sQuery(id+"F0.wireOp",EDGE,"E14.18.21.0"),sQuery(id+"F0.wireOp",EDGE,"E14.22.21.0"),sQuery(id+"F0.wireOp",EDGE,"E14.26.21.0"),sQuery(id+"F0.wireOp",EDGE,"E14.29.21.0"),sQuery(id+"F0.wireOp",EDGE,"E14.1.22.0"),sQuery(id+"F0.wireOp",EDGE,"E14.4.22.0"),sQuery(id+"F0.wireOp",EDGE,"E14.7.22.0"),sQuery(id+"F0.wireOp",EDGE,"E14.11.22.0"),sQuery(id+"F0.wireOp",EDGE,"E14.15.22.0"),sQuery(id+"F0.wireOp",EDGE,"E14.18.22.0"),sQuery(id+"F0.wireOp",EDGE,"E14.22.22.0"),sQuery(id+"F0.wireOp",EDGE,"E14.26.22.0"),sQuery(id+"F0.wireOp",EDGE,"E14.29.22.0"),sQuery(id+"F0.wireOp",EDGE,"E14.1.23.0"),sQuery(id+"F0.wireOp",EDGE,"E14.4.23.0"),sQuery(id+"F0.wireOp",EDGE,"E14.7.23.0"),sQuery(id+"F0.wireOp",EDGE,"E14.11.23.0"),sQuery(id+"F0.wireOp",EDGE,"E14.15.23.0"),sQuery(id+"F0.wireOp",EDGE,"E14.18.23.0"),sQuery(id+"F0.wireOp",EDGE,"E14.22.23.0"),sQuery(id+"F0.wireOp",EDGE,"E14.26.23.0"),sQuery(id+"F0.wireOp",EDGE,"E14.29.23.0"),sQuery(id+"F0.wireOp",EDGE,"E14.1.24.0"),sQuery(id+"F0.wireOp",EDGE,"E14.4.24.0"),sQuery(id+"F0.wireOp",EDGE,"E14.7.24.0"),sQuery(id+"F0.wireOp",EDGE,"E14.11.24.0"),sQuery(id+"F0.wireOp",EDGE,"E14.15.24.0"),sQuery(id+"F0.wireOp",EDGE,"E14.18.24.0"),sQuery(id+"F0.wireOp",EDGE,"E14.22.24.0"),sQuery(id+"F0.wireOp",EDGE,"E14.26.24.0"),sQuery(id+"F0.wireOp",EDGE,"E14.29.24.0"),sQuery(id+"F0.wireOp",EDGE,"E14.1.25.0"),sQuery(id+"F0.wireOp",EDGE,"E14.4.25.0"),sQuery(id+"F0.wireOp",EDGE,"E14.7.25.0"),sQuery(id+"F0.wireOp",EDGE,"E14.11.25.0"),sQuery(id+"F0.wireOp",EDGE,"E14.15.25.0"),sQuery(id+"F0.wireOp",EDGE,"E14.18.25.0"),sQuery(id+"F0.wireOp",EDGE,"E14.22.25.0"),sQuery(id+"F0.wireOp",EDGE,"E14.26.25.0"),sQuery(id+"F0.wireOp",EDGE,"E14.29.25.0"),sQuery(id+"F0.wireOp",EDGE,"E14.1.26.0"),sQuery(id+"F0.wireOp",EDGE,"E14.4.26.0"),sQuery(id+"F0.wireOp",EDGE,"E14.7.26.0"),sQuery(id+"F0.wireOp",EDGE,"E14.11.26.0"),sQuery(id+"F0.wireOp",EDGE,"E14.15.26.0"),sQuery(id+"F0.wireOp",EDGE,"E14.18.26.0"),sQuery(id+"F0.wireOp",EDGE,"E14.22.26.0"),sQuery(id+"F0.wireOp",EDGE,"E14.26.26.0"),sQuery(id+"F0.wireOp",EDGE,"E14.29.26.0"),sQuery(id+"F0.wireOp",EDGE,"E14.1.27.0"),sQuery(id+"F0.wireOp",EDGE,"E14.4.27.0"),sQuery(id+"F0.wireOp",EDGE,"E14.7.27.0"),sQuery(id+"F0.wireOp",EDGE,"E14.11.27.0"),sQuery(id+"F0.wireOp",EDGE,"E14.15.27.0"),sQuery(id+"F0.wireOp",EDGE,"E14.18.27.0"),sQuery(id+"F0.wireOp",EDGE,"E14.22.27.0"),sQuery(id+"F0.wireOp",EDGE,"E14.26.27.0"),sQuery(id+"F0.wireOp",EDGE,"E14.29.27.0"),sQuery(id+"F0.wireOp",EDGE,"E14.1.28.0"),sQuery(id+"F0.wireOp",EDGE,"E14.4.28.0"),sQuery(id+"F0.wireOp",EDGE,"E14.7.28.0"),sQuery(id+"F0.wireOp",EDGE,"E14.11.28.0"),sQuery(id+"F0.wireOp",EDGE,"E14.15.28.0"),sQuery(id+"F0.wireOp",EDGE,"E14.18.28.0"),sQuery(id+"F0.wireOp",EDGE,"E14.22.28.0"),sQuery(id+"F0.wireOp",EDGE,"E14.26.28.0"),sQuery(id+"F0.wireOp",EDGE,"E14.29.28.0"),sQuery(id+"F0.wireOp",EDGE,"E14.1.29.0"),sQuery(id+"F0.wireOp",EDGE,"E14.4.29.0"),sQuery(id+"F0.wireOp",EDGE,"E14.7.29.0"),sQuery(id+"F0.wireOp",EDGE,"E14.11.29.0"),sQuery(id+"F0.wireOp",EDGE,"E14.15.29.0"),sQuery(id+"F0.wireOp",EDGE,"E14.18.29.0"),sQuery(id+"F0.wireOp",EDGE,"E14.22.29.0"),sQuery(id+"F0.wireOp",EDGE,"E14.26.29.0"),sQuery(id+"F0.wireOp",EDGE,"E14.29.29.0"),sQuery(id+"F0.wireOp",EDGE,"E14.1.30.0"),sQuery(id+"F0.wireOp",EDGE,"E14.4.30.0"),sQuery(id+"F0.wireOp",EDGE,"E14.7.30.0"),sQuery(id+"F0.wireOp",EDGE,"E14.11.30.0"),sQuery(id+"F0.wireOp",EDGE,"E14.15.30.0"),sQuery(id+"F0.wireOp",EDGE,"E14.18.30.0"),sQuery(id+"F0.wireOp",EDGE,"E14.22.30.0"),sQuery(id+"F0.wireOp",EDGE,"E14.26.30.0"),sQuery(id+"F0.wireOp",EDGE,"E14.29.30.0"),sQuery(id+"F0.wireOp",EDGE,"E14.1.31.0"),sQuery(id+"F0.wireOp",EDGE,"E14.4.31.0"),sQuery(id+"F0.wireOp",EDGE,"E14.7.31.0"),sQuery(id+"F0.wireOp",EDGE,"E14.11.31.0"),sQuery(id+"F0.wireOp",EDGE,"E14.15.31.0"),sQuery(id+"F0.wireOp",EDGE,"E14.18.31.0"),sQuery(id+"F0.wireOp",EDGE,"E14.22.31.0"),sQuery(id+"F0.wireOp",EDGE,"E14.26.31.0"),sQuery(id+"F0.wireOp",EDGE,"E14.29.31.0"),sQuery(id+"F0.wireOp",EDGE,"E14.1.32.0"),sQuery(id+"F0.wireOp",EDGE,"E14.4.32.0"),sQuery(id+"F0.wireOp",EDGE,"E14.7.32.0"),sQuery(id+"F0.wireOp",EDGE,"E14.11.32.0"),sQuery(id+"F0.wireOp",EDGE,"E14.15.32.0"),sQuery(id+"F0.wireOp",EDGE,"E14.18.32.0"),sQuery(id+"F0.wireOp",EDGE,"E14.22.32.0"),sQuery(id+"F0.wireOp",EDGE,"E14.26.32.0"),sQuery(id+"F0.wireOp",EDGE,"E14.29.32.0"),sQuery(id+"F0.wireOp",EDGE,"E14.1.33.0"),sQuery(id+"F0.wireOp",EDGE,"E14.4.33.0"),sQuery(id+"F0.wireOp",EDGE,"E14.7.33.0"),sQuery(id+"F0.wireOp",EDGE,"E14.11.33.0"),sQuery(id+"F0.wireOp",EDGE,"E14.15.33.0"),sQuery(id+"F0.wireOp",EDGE,"E14.18.33.0"),sQuery(id+"F0.wireOp",EDGE,"E14.22.33.0"),sQuery(id+"F0.wireOp",EDGE,"E14.26.33.0"),sQuery(id+"F0.wireOp",EDGE,"E14.29.33.0"),sQuery(id+"F0.wireOp",EDGE,"E14.1.34.0"),sQuery(id+"F0.wireOp",EDGE,"E14.4.34.0"),sQuery(id+"F0.wireOp",EDGE,"E14.7.34.0"),sQuery(id+"F0.wireOp",EDGE,"E14.11.34.0"),sQuery(id+"F0.wireOp",EDGE,"E14.15.34.0"),sQuery(id+"F0.wireOp",EDGE,"E14.18.34.0"),sQuery(id+"F0.wireOp",EDGE,"E14.22.34.0"),sQuery(id+"F0.wireOp",EDGE,"E14.26.34.0"),sQuery(id+"F0.wireOp",EDGE,"E14.29.34.0"),sQuery(id+"F0.wireOp",EDGE,"E14.1.35.0"),sQuery(id+"F0.wireOp",EDGE,"E14.4.35.0"),sQuery(id+"F0.wireOp",EDGE,"E14.7.35.0"),sQuery(id+"F0.wireOp",EDGE,"E14.11.35.0"),sQuery(id+"F0.wireOp",EDGE,"E14.15.35.0"),sQuery(id+"F0.wireOp",EDGE,"E14.18.35.0"),sQuery(id+"F0.wireOp",EDGE,"E14.22.35.0"),sQuery(id+"F0.wireOp",EDGE,"E14.26.35.0"),sQuery(id+"F0.wireOp",EDGE,"E14.29.35.0"),sQuery(id+"F0.wireOp",EDGE,"E14.1.36.0"),sQuery(id+"F0.wireOp",EDGE,"E14.4.36.0"),sQuery(id+"F0.wireOp",EDGE,"E14.7.36.0"),sQuery(id+"F0.wireOp",EDGE,"E14.11.36.0"),sQuery(id+"F0.wireOp",EDGE,"E14.15.36.0"),sQuery(id+"F0.wireOp",EDGE,"E14.18.36.0"),sQuery(id+"F0.wireOp",EDGE,"E14.22.36.0"),sQuery(id+"F0.wireOp",EDGE,"E14.26.36.0"),sQuery(id+"F0.wireOp",EDGE,"E14.29.36.0"),sQuery(id+"F0.wireOp",EDGE,"E14.1.37.0"),sQuery(id+"F0.wireOp",EDGE,"E14.4.37.0"),sQuery(id+"F0.wireOp",EDGE,"E14.7.37.0"),sQuery(id+"F0.wireOp",EDGE,"E14.11.37.0"),sQuery(id+"F0.wireOp",EDGE,"E14.15.37.0"),sQuery(id+"F0.wireOp",EDGE,"E14.18.37.0"),sQuery(id+"F0.wireOp",EDGE,"E14.22.37.0"),sQuery(id+"F0.wireOp",EDGE,"E14.26.37.0"),sQuery(id+"F0.wireOp",EDGE,"E14.29.37.0"),sQuery(id+"F0.wireOp",EDGE,"E14.1.38.0"),sQuery(id+"F0.wireOp",EDGE,"E14.4.38.0"),sQuery(id+"F0.wireOp",EDGE,"E14.7.38.0"),sQuery(id+"F0.wireOp",EDGE,"E14.11.38.0"),sQuery(id+"F0.wireOp",EDGE,"E14.15.38.0"),sQuery(id+"F0.wireOp",EDGE,"E14.18.38.0"),sQuery(id+"F0.wireOp",EDGE,"E14.22.38.0"),sQuery(id+"F0.wireOp",EDGE,"E14.26.38.0"),sQuery(id+"F0.wireOp",EDGE,"E14.29.38.0"),sQuery(id+"F0.wireOp",EDGE,"E14.1.39.0"),sQuery(id+"F0.wireOp",EDGE,"E14.4.39.0"),sQuery(id+"F0.wireOp",EDGE,"E14.7.39.0"),sQuery(id+"F0.wireOp",EDGE,"E14.11.39.0"),sQuery(id+"F0.wireOp",EDGE,"E14.15.39.0"),sQuery(id+"F0.wireOp",EDGE,"E14.18.39.0"),sQuery(id+"F0.wireOp",EDGE,"E14.22.39.0"),sQuery(id+"F0.wireOp",EDGE,"E14.26.39.0"),sQuery(id+"F0.wireOp",EDGE,"E14.29.39.0"),sQuery(id+"F0.wireOp",EDGE,"E14.1.40.0"),sQuery(id+"F0.wireOp",EDGE,"E14.4.40.0"),sQuery(id+"F0.wireOp",EDGE,"E14.7.40.0"),sQuery(id+"F0.wireOp",EDGE,"E14.11.40.0"),sQuery(id+"F0.wireOp",EDGE,"E14.15.40.0"),sQuery(id+"F0.wireOp",EDGE,"E14.18.40.0"),sQuery(id+"F0.wireOp",EDGE,"E14.22.40.0"),sQuery(id+"F0.wireOp",EDGE,"E14.26.40.0"),sQuery(id+"F0.wireOp",EDGE,"E14.29.40.0"),sQuery(id+"F0.wireOp",EDGE,"E14.1.41.0"),sQuery(id+"F0.wireOp",EDGE,"E14.4.41.0"),sQuery(id+"F0.wireOp",EDGE,"E14.7.41.0"),sQuery(id+"F0.wireOp",EDGE,"E14.11.41.0"),sQuery(id+"F0.wireOp",EDGE,"E14.15.41.0"),sQuery(id+"F0.wireOp",EDGE,"E14.18.41.0"),sQuery(id+"F0.wireOp",EDGE,"E14.22.41.0"),sQuery(id+"F0.wireOp",EDGE,"E14.26.41.0"),sQuery(id+"F0.wireOp",EDGE,"E14.29.41.0"),sQuery(id+"F0.wireOp",EDGE,"E14.1.42.0"),sQuery(id+"F0.wireOp",EDGE,"E14.4.42.0"),sQuery(id+"F0.wireOp",EDGE,"E14.7.42.0"),sQuery(id+"F0.wireOp",EDGE,"E14.11.42.0"),sQuery(id+"F0.wireOp",EDGE,"E14.15.42.0"),sQuery(id+"F0.wireOp",EDGE,"E14.18.42.0"),sQuery(id+"F0.wireOp",EDGE,"E14.22.42.0"),sQuery(id+"F0.wireOp",EDGE,"E14.26.42.0"),sQuery(id+"F0.wireOp",EDGE,"E14.29.42.0"),sQuery(id+"F0.wireOp",EDGE,"E14.1.43.0"),sQuery(id+"F0.wireOp",EDGE,"E14.4.43.0"),sQuery(id+"F0.wireOp",EDGE,"E14.7.43.0"),sQuery(id+"F0.wireOp",EDGE,"E14.11.43.0"),sQuery(id+"F0.wireOp",EDGE,"E14.15.43.0"),sQuery(id+"F0.wireOp",EDGE,"E14.18.43.0"),sQuery(id+"F0.wireOp",EDGE,"E14.22.43.0"),sQuery(id+"F0.wireOp",EDGE,"E14.26.43.0"),sQuery(id+"F0.wireOp",EDGE,"E14.29.43.0"),sQuery(id+"F0.wireOp",EDGE,"E14.1.44.0"),sQuery(id+"F0.wireOp",EDGE,"E14.4.44.0"),sQuery(id+"F0.wireOp",EDGE,"E14.7.44.0"),sQuery(id+"F0.wireOp",EDGE,"E14.11.44.0"),sQuery(id+"F0.wireOp",EDGE,"E14.15.44.0"),sQuery(id+"F0.wireOp",EDGE,"E14.18.44.0"),sQuery(id+"F0.wireOp",EDGE,"E14.22.44.0"),sQuery(id+"F0.wireOp",EDGE,"E14.26.44.0"),sQuery(id+"F0.wireOp",EDGE,"E14.29.44.0"),sQuery(id+"F0.wireOp",EDGE,"E14.1.45.0"),sQuery(id+"F0.wireOp",EDGE,"E14.4.45.0"),sQuery(id+"F0.wireOp",EDGE,"E14.7.45.0"),sQuery(id+"F0.wireOp",EDGE,"E14.11.45.0"),sQuery(id+"F0.wireOp",EDGE,"E14.15.45.0"),sQuery(id+"F0.wireOp",EDGE,"E14.18.45.0"),sQuery(id+"F0.wireOp",EDGE,"E14.22.45.0"),sQuery(id+"F0.wireOp",EDGE,"E14.26.45.0"),sQuery(id+"F0.wireOp",EDGE,"E14.29.45.0"),sQuery(id+"F0.wireOp",EDGE,"E14.1.46.0"),sQuery(id+"F0.wireOp",EDGE,"E14.4.46.0"),sQuery(id+"F0.wireOp",EDGE,"E14.7.46.0"),sQuery(id+"F0.wireOp",EDGE,"E14.11.46.0"),sQuery(id+"F0.wireOp",EDGE,"E14.15.46.0"),sQuery(id+"F0.wireOp",EDGE,"E14.18.46.0"),sQuery(id+"F0.wireOp",EDGE,"E14.22.46.0"),sQuery(id+"F0.wireOp",EDGE,"E14.26.46.0"),sQuery(id+"F0.wireOp",EDGE,"E14.29.46.0"),sQuery(id+"F0.wireOp",EDGE,"E14.1.47.0"),sQuery(id+"F0.wireOp",EDGE,"E14.4.47.0"),sQuery(id+"F0.wireOp",EDGE,"E14.7.47.0"),sQuery(id+"F0.wireOp",EDGE,"E14.11.47.0"),sQuery(id+"F0.wireOp",EDGE,"E14.15.47.0"),sQuery(id+"F0.wireOp",EDGE,"E14.18.47.0"),sQuery(id+"F0.wireOp",EDGE,"E14.22.47.0"),sQuery(id+"F0.wireOp",EDGE,"E14.26.47.0"),sQuery(id+"F0.wireOp",EDGE,"E14.29.47.0"),sQuery(id+"F0.wireOp",EDGE,"E14.1.48.0"),sQuery(id+"F0.wireOp",EDGE,"E14.4.48.0"),sQuery(id+"F0.wireOp",EDGE,"E14.7.48.0"),sQuery(id+"F0.wireOp",EDGE,"E14.11.48.0"),sQuery(id+"F0.wireOp",EDGE,"E14.15.48.0"),sQuery(id+"F0.wireOp",EDGE,"E14.18.48.0"),sQuery(id+"F0.wireOp",EDGE,"E14.22.48.0"),sQuery(id+"F0.wireOp",EDGE,"E14.26.48.0"),sQuery(id+"F0.wireOp",EDGE,"E14.29.48.0"),sQuery(id+"F0.wireOp",EDGE,"E14.1.49.0"),sQuery(id+"F0.wireOp",EDGE,"E14.4.49.0"),sQuery(id+"F0.wireOp",EDGE,"E14.7.49.0"),sQuery(id+"F0.wireOp",EDGE,"E14.11.49.0"),sQuery(id+"F0.wireOp",EDGE,"E14.15.49.0"),sQuery(id+"F0.wireOp",EDGE,"E14.18.49.0"),sQuery(id+"F0.wireOp",EDGE,"E14.22.49.0"),sQuery(id+"F0.wireOp",EDGE,"E14.26.49.0"),sQuery(id+"F0.wireOp",EDGE,"E14.29.49.0"),sQuery(id+"F0.wireOp",EDGE,"E14.1.50.0"),sQuery(id+"F0.wireOp",EDGE,"E14.4.50.0"),sQuery(id+"F0.wireOp",EDGE,"E14.7.50.0"),sQuery(id+"F0.wireOp",EDGE,"E14.11.50.0"),sQuery(id+"F0.wireOp",EDGE,"E14.15.50.0"),sQuery(id+"F0.wireOp",EDGE,"E14.18.50.0"),sQuery(id+"F0.wireOp",EDGE,"E14.22.50.0"),sQuery(id+"F0.wireOp",EDGE,"E14.26.50.0"),sQuery(id+"F0.wireOp",EDGE,"E14.29.50.0"),sQuery(id+"F0.wireOp",EDGE,"E14.1.51.0"),sQuery(id+"F0.wireOp",EDGE,"E14.4.51.0"),sQuery(id+"F0.wireOp",EDGE,"E14.7.51.0"),sQuery(id+"F0.wireOp",EDGE,"E14.11.51.0"),sQuery(id+"F0.wireOp",EDGE,"E14.15.51.0"),sQuery(id+"F0.wireOp",EDGE,"E14.18.51.0"),sQuery(id+"F0.wireOp",EDGE,"E14.22.51.0"),sQuery(id+"F0.wireOp",EDGE,"E14.26.51.0"),sQuery(id+"F0.wireOp",EDGE,"E14.29.51.0"),sQuery(id+"F0.wireOp",EDGE,"E14.1.52.0"),sQuery(id+"F0.wireOp",EDGE,"E14.4.52.0"),sQuery(id+"F0.wireOp",EDGE,"E14.7.52.0"),sQuery(id+"F0.wireOp",EDGE,"E14.11.52.0"),sQuery(id+"F0.wireOp",EDGE,"E14.15.52.0"),sQuery(id+"F0.wireOp",EDGE,"E14.18.52.0"),sQuery(id+"F0.wireOp",EDGE,"E14.22.52.0"),sQuery(id+"F0.wireOp",EDGE,"E14.26.52.0"),sQuery(id+"F0.wireOp",EDGE,"E14.29.52.0"),sQuery(id+"F0.wireOp",EDGE,"E14.1.53.0"),sQuery(id+"F0.wireOp",EDGE,"E14.4.53.0"),sQuery(id+"F0.wireOp",EDGE,"E14.7.53.0"),sQuery(id+"F0.wireOp",EDGE,"E14.11.53.0"),sQuery(id+"F0.wireOp",EDGE,"E14.15.53.0"),sQuery(id+"F0.wireOp",EDGE,"E14.18.53.0"),sQuery(id+"F0.wireOp",EDGE,"E14.22.53.0"),sQuery(id+"F0.wireOp",EDGE,"E14.26.53.0"),sQuery(id+"F0.wireOp",EDGE,"E14.29.53.0"),sQuery(id+"F0.wireOp",EDGE,"E14.1.54.0"),sQuery(id+"F0.wireOp",EDGE,"E14.4.54.0"),sQuery(id+"F0.wireOp",EDGE,"E14.7.54.0"),sQuery(id+"F0.wireOp",EDGE,"E14.11.54.0"),sQuery(id+"F0.wireOp",EDGE,"E14.15.54.0"),sQuery(id+"F0.wireOp",EDGE,"E14.18.54.0"),sQuery(id+"F0.wireOp",EDGE,"E14.22.54.0"),sQuery(id+"F0.wireOp",EDGE,"E14.26.54.0"),sQuery(id+"F0.wireOp",EDGE,"E14.29.54.0"),sQuery(id+"F0.wireOp",EDGE,"E14.1.55.0"),sQuery(id+"F0.wireOp",EDGE,"E14.4.55.0"),sQuery(id+"F0.wireOp",EDGE,"E14.7.55.0"),sQuery(id+"F0.wireOp",EDGE,"E14.11.55.0"),sQuery(id+"F0.wireOp",EDGE,"E14.15.55.0"),sQuery(id+"F0.wireOp",EDGE,"E14.18.55.0"),sQuery(id+"F0.wireOp",EDGE,"E14.22.55.0"),sQuery(id+"F0.wireOp",EDGE,"E14.26.55.0"),sQuery(id+"F0.wireOp",EDGE,"E14.29.55.0"),sQuery(id+"F0.wireOp",EDGE,"E14.1.56.0"),sQuery(id+"F0.wireOp",EDGE,"E14.4.56.0"),sQuery(id+"F0.wireOp",EDGE,"E14.7.56.0"),sQuery(id+"F0.wireOp",EDGE,"E14.11.56.0"),sQuery(id+"F0.wireOp",EDGE,"E14.15.56.0"),sQuery(id+"F0.wireOp",EDGE,"E14.18.56.0"),sQuery(id+"F0.wireOp",EDGE,"E14.22.56.0"),sQuery(id+"F0.wireOp",EDGE,"E14.26.56.0"),sQuery(id+"F0.wireOp",EDGE,"E14.29.56.0"),sQuery(id+"F0.wireOp",EDGE,"E14.1.57.0"),sQuery(id+"F0.wireOp",EDGE,"E14.4.57.0"),sQuery(id+"F0.wireOp",EDGE,"E14.7.57.0"),sQuery(id+"F0.wireOp",EDGE,"E14.11.57.0"),sQuery(id+"F0.wireOp",EDGE,"E14.15.57.0"),sQuery(id+"F0.wireOp",EDGE,"E14.18.57.0"),sQuery(id+"F0.wireOp",EDGE,"E14.22.57.0"),sQuery(id+"F0.wireOp",EDGE,"E14.26.57.0"),sQuery(id+"F0.wireOp",EDGE,"E14.29.57.0"),sQuery(id+"F0.wireOp",EDGE,"E14.1.58.0"),sQuery(id+"F0.wireOp",EDGE,"E14.4.58.0"),sQuery(id+"F0.wireOp",EDGE,"E14.7.58.0"),sQuery(id+"F0.wireOp",EDGE,"E14.11.58.0"),sQuery(id+"F0.wireOp",EDGE,"E14.15.58.0"),sQuery(id+"F0.wireOp",EDGE,"E14.18.58.0"),sQuery(id+"F0.wireOp",EDGE,"E14.22.58.0"),sQuery(id+"F0.wireOp",EDGE,"E14.26.58.0"),sQuery(id+"F0.wireOp",EDGE,"E14.29.58.0"),sQuery(id+"F0.wireOp",EDGE,"E14.1.59.0"),sQuery(id+"F0.wireOp",EDGE,"E14.4.59.0"),sQuery(id+"F0.wireOp",EDGE,"E14.7.59.0"),sQuery(id+"F0.wireOp",EDGE,"E14.11.59.0"),sQuery(id+"F0.wireOp",EDGE,"E14.15.59.0"),sQuery(id+"F0.wireOp",EDGE,"E14.18.59.0"),sQuery(id+"F0.wireOp",EDGE,"E14.22.59.0"),sQuery(id+"F0.wireOp",EDGE,"E14.26.59.0"),sQuery(id+"F0.wireOp",EDGE,"E14.29.59.0"),sQuery(id+"F0.wireOp",EDGE,"E14.1.60.0"),sQuery(id+"F0.wireOp",EDGE,"E14.4.60.0"),sQuery(id+"F0.wireOp",EDGE,"E14.7.60.0"),sQuery(id+"F0.wireOp",EDGE,"E14.11.60.0"),sQuery(id+"F0.wireOp",EDGE,"E14.15.60.0"),sQuery(id+"F0.wireOp",EDGE,"E14.18.60.0"),sQuery(id+"F0.wireOp",EDGE,"E14.22.60.0"),sQuery(id+"F0.wireOp",EDGE,"E14.26.60.0"),sQuery(id+"F0.wireOp",EDGE,"E14.29.60.0"),sQuery(id+"F0.wireOp",EDGE,"E14.1.61.0"),sQuery(id+"F0.wireOp",EDGE,"E14.4.61.0"),sQuery(id+"F0.wireOp",EDGE,"E14.7.61.0"),sQuery(id+"F0.wireOp",EDGE,"E14.11.61.0"),sQuery(id+"F0.wireOp",EDGE,"E14.15.61.0"),sQuery(id+"F0.wireOp",EDGE,"E14.18.61.0"),sQuery(id+"F0.wireOp",EDGE,"E14.22.61.0"),sQuery(id+"F0.wireOp",EDGE,"E14.26.61.0"),sQuery(id+"F0.wireOp",EDGE,"E14.29.61.0"),sQuery(id+"F0.wireOp",EDGE,"E14.1.62.0"),sQuery(id+"F0.wireOp",EDGE,"E14.4.62.0"),sQuery(id+"F0.wireOp",EDGE,"E14.7.62.0"),sQuery(id+"F0.wireOp",EDGE,"E14.11.62.0"),sQuery(id+"F0.wireOp",EDGE,"E14.15.62.0"),sQuery(id+"F0.wireOp",EDGE,"E14.18.62.0"),sQuery(id+"F0.wireOp",EDGE,"E14.22.62.0"),sQuery(id+"F0.wireOp",EDGE,"E14.26.62.0"),sQuery(id+"F0.wireOp",EDGE,"E14.29.62.0"),sQuery(id+"F0.wireOp",EDGE,"E14.1.63.0"),sQuery(id+"F0.wireOp",EDGE,"E14.4.63.0"),sQuery(id+"F0.wireOp",EDGE,"E14.7.63.0"),sQuery(id+"F0.wireOp",EDGE,"E14.11.63.0"),sQuery(id+"F0.wireOp",EDGE,"E14.15.63.0"),sQuery(id+"F0.wireOp",EDGE,"E14.18.63.0"),sQuery(id+"F0.wireOp",EDGE,"E14.22.63.0"),sQuery(id+"F0.wireOp",EDGE,"E14.26.63.0"),sQuery(id+"F0.wireOp",EDGE,"E14.29.63.0"),sQuery(id+"F0.wireOp",EDGE,"E14.1.64.0"),sQuery(id+"F0.wireOp",EDGE,"E14.4.64.0"),sQuery(id+"F0.wireOp",EDGE,"E14.7.64.0"),sQuery(id+"F0.wireOp",EDGE,"E14.11.64.0"),sQuery(id+"F0.wireOp",EDGE,"E14.15.64.0"),sQuery(id+"F0.wireOp",EDGE,"E14.18.64.0"),sQuery(id+"F0.wireOp",EDGE,"E14.22.64.0"),sQuery(id+"F0.wireOp",EDGE,"E14.26.64.0"),sQuery(id+"F0.wireOp",EDGE,"E14.29.64.0"),sQuery(id+"F0.wireOp",EDGE,"E14.1.65.0"),sQuery(id+"F0.wireOp",EDGE,"E14.4.65.0"),sQuery(id+"F0.wireOp",EDGE,"E14.7.65.0"),sQuery(id+"F0.wireOp",EDGE,"E14.11.65.0"),sQuery(id+"F0.wireOp",EDGE,"E14.15.65.0"),sQuery(id+"F0.wireOp",EDGE,"E14.18.65.0"),sQuery(id+"F0.wireOp",EDGE,"E14.22.65.0"),sQuery(id+"F0.wireOp",EDGE,"E14.26.65.0"),sQuery(id+"F0.wireOp",EDGE,"E14.29.65.0"),sQuery(id+"F0.wireOp",EDGE,"E14.1.66.0"),sQuery(id+"F0.wireOp",EDGE,"E14.4.66.0"),sQuery(id+"F0.wireOp",EDGE,"E14.7.66.0"),sQuery(id+"F0.wireOp",EDGE,"E14.11.66.0"),sQuery(id+"F0.wireOp",EDGE,"E14.15.66.0"),sQuery(id+"F0.wireOp",EDGE,"E14.18.66.0"),sQuery(id+"F0.wireOp",EDGE,"E14.22.66.0"),sQuery(id+"F0.wireOp",EDGE,"E14.26.66.0"),sQuery(id+"F0.wireOp",EDGE,"E14.29.66.0"),sQuery(id+"F0.wireOp",EDGE,"E14.1.67.0"),sQuery(id+"F0.wireOp",EDGE,"E14.4.67.0"),sQuery(id+"F0.wireOp",EDGE,"E14.7.67.0"),sQuery(id+"F0.wireOp",EDGE,"E14.11.67.0"),sQuery(id+"F0.wireOp",EDGE,"E14.15.67.0"),sQuery(id+"F0.wireOp",EDGE,"E14.18.67.0"),sQuery(id+"F0.wireOp",EDGE,"E14.22.67.0"),sQuery(id+"F0.wireOp",EDGE,"E14.26.67.0"),sQuery(id+"F0.wireOp",EDGE,"E14.29.67.0"),sQuery(id+"F0.wireOp",EDGE,"E14.1.68.0"),sQuery(id+"F0.wireOp",EDGE,"E14.4.68.0"),sQuery(id+"F0.wireOp",EDGE,"E14.7.68.0"),sQuery(id+"F0.wireOp",EDGE,"E14.11.68.0"),sQuery(id+"F0.wireOp",EDGE,"E14.15.68.0"),sQuery(id+"F0.wireOp",EDGE,"E14.18.68.0"),sQuery(id+"F0.wireOp",EDGE,"E14.22.68.0"),sQuery(id+"F0.wireOp",EDGE,"E14.26.68.0"),sQuery(id+"F0.wireOp",EDGE,"E14.29.68.0"),sQuery(id+"F0.wireOp",EDGE,"E14.1.69.0"),sQuery(id+"F0.wireOp",EDGE,"E14.4.69.0"),sQuery(id+"F0.wireOp",EDGE,"E14.7.69.0"),sQuery(id+"F0.wireOp",EDGE,"E14.11.69.0"),sQuery(id+"F0.wireOp",EDGE,"E14.15.69.0"),sQuery(id+"F0.wireOp",EDGE,"E14.18.69.0"),sQuery(id+"F0.wireOp",EDGE,"E14.22.69.0"),sQuery(id+"F0.wireOp",EDGE,"E14.26.69.0"),sQuery(id+"F0.wireOp",EDGE,"E14.29.69.0"),sQuery(id+"F0.wireOp",EDGE,"E14.1.70.0"),sQuery(id+"F0.wireOp",EDGE,"E14.4.70.0"),sQuery(id+"F0.wireOp",EDGE,"E14.7.70.0"),sQuery(id+"F0.wireOp",EDGE,"E14.11.70.0"),sQuery(id+"F0.wireOp",EDGE,"E14.15.70.0"),sQuery(id+"F0.wireOp",EDGE,"E14.18.70.0"),sQuery(id+"F0.wireOp",EDGE,"E14.22.70.0"),sQuery(id+"F0.wireOp",EDGE,"E14.26.70.0"),sQuery(id+"F0.wireOp",EDGE,"E14.29.70.0"),sQuery(id+"F0.wireOp",EDGE,"E14.1.71.0"),sQuery(id+"F0.wireOp",EDGE,"E14.4.71.0"),sQuery(id+"F0.wireOp",EDGE,"E14.7.71.0"),sQuery(id+"F0.wireOp",EDGE,"E14.11.71.0"),sQuery(id+"F0.wireOp",EDGE,"E14.15.71.0"),sQuery(id+"F0.wireOp",EDGE,"E14.18.71.0"),sQuery(id+"F0.wireOp",EDGE,"E14.22.71.0"),sQuery(id+"F0.wireOp",EDGE,"E14.26.71.0"),sQuery(id+"F0.wireOp",EDGE,"E14.29.71.0"),sQuery(id+"F0.wireOp",EDGE,"E15.trimOffspring"),sQuery(id+"F0.wireOp",EDGE,"E16.trimOffspring"),sQuery(id+"F0.wireOp",EDGE,"E17.trimOffspring"),sQuery(id+"F0.wireOp",EDGE,"E18.trimOffspring"),sQuery(id+"F0.wireOp",EDGE,"E19.trimOffspring"),sQuery(id+"F0.wireOp",EDGE,"E20.trimOffspring"),sQuery(id+"F0.wireOp",EDGE,"E21.trimOffspring"),sQuery(id+"F0.wireOp",EDGE,"E22.trimOffspring"),sQuery(id+"F0.wireOp",EDGE,"E23.trimOffspring"),sQuery(id+"F0.wireOp",EDGE,"E24.trimOffspring"),sQuery(id+"F0.wireOp",EDGE,"E25.trimOffspring"),sQuery(id+"F0.wireOp",EDGE,"E26.trimOffspring"),sQuery(id+"F0.wireOp",EDGE,"E27.trimOffspring"),sQuery(id+"F0.wireOp",EDGE,"E28.trimOffspring"),sQuery(id+"F0.wireOp",EDGE,"E29.trimOffspring"),sQuery(id+"F0.wireOp",EDGE,"E30.trimOffspring"),sQuery(id+"F0.wireOp",EDGE,"E31.trimOffspring"),sQuery(id+"F0.wireOp",EDGE,"E32.trimOffspring"),sQuery(id+"F0.wireOp",EDGE,"E33.trimOffspring"),sQuery(id+"F0.wireOp",EDGE,"E34.trimOffspring"),sQuery(id+"F0.wireOp",EDGE,"E35.trimOffspring"),sQuery(id+"F0.wireOp",EDGE,"E36.trimOffspring"),sQuery(id+"F0.wireOp",EDGE,"E37.trimOffspring"),sQuery(id+"F0.wireOp",EDGE,"E38.trimOffspring"),sQuery(id+"F0.wireOp",EDGE,"E39.trimOffspring"),sQuery(id+"F0.wireOp",EDGE,"E40.trimOffspring"),sQuery(id+"F0.wireOp",EDGE,"E41.trimOffspring"),sQuery(id+"F0.wireOp",EDGE,"E42.trimOffspring"),sQuery(id+"F0.wireOp",EDGE,"E43.trimOffspring"),sQuery(id+"F0.wireOp",EDGE,"E44.trimOffspring"),sQuery(id+"F0.wireOp",EDGE,"E45.trimOffspring"),sQuery(id+"F0.wireOp",EDGE,"E46.trimOffspring"),sQuery(id+"F0.wireOp",EDGE,"E47.trimOffspring"),sQuery(id+"F0.wireOp",EDGE,"E48.trimOffspring"),sQuery(id+"F0.wireOp",EDGE,"E49.trimOffspring"),sQuery(id+"F0.wireOp",EDGE,"E50.trimOffspring"),sQuery(id+"F0.wireOp",EDGE,"E51.trimOffspring"),sQuery(id+"F0.wireOp",EDGE,"E52.trimOffspring"),sQuery(id+"F0.wireOp",EDGE,"E53.trimOffspring"),sQuery(id+"F0.wireOp",EDGE,"E54.trimOffspring"),sQuery(id+"F0.wireOp",EDGE,"E55.trimOffspring"),sQuery(id+"F0.wireOp",EDGE,"E56.trimOffspring"),sQuery(id+"F0.wireOp",EDGE,"E57.trimOffspring"),sQuery(id+"F0.wireOp",EDGE,"E58.trimOffspring"),sQuery(id+"F0.wireOp",EDGE,"E59.trimOffspring"),sQuery(id+"F0.wireOp",EDGE,"E60.trimOffspring"),sQuery(id+"F0.wireOp",EDGE,"E61.trimOffspring"),sQuery(id+"F0.wireOp",EDGE,"E62.trimOffspring"),sQuery(id+"F0.wireOp",EDGE,"E63.trimOffspring"),sQuery(id+"F0.wireOp",EDGE,"E64.trimOffspring"),sQuery(id+"F0.wireOp",EDGE,"E65.trimOffspring"),sQuery(id+"F0.wireOp",EDGE,"E66.trimOffspring"),sQuery(id+"F0.wireOp",EDGE,"E67.trimOffspring"),sQuery(id+"F0.wireOp",EDGE,"E68.trimOffspring"),sQuery(id+"F0.wireOp",EDGE,"E69.trimOffspring"),sQuery(id+"F0.wireOp",EDGE,"E70.trimOffspring"),sQuery(id+"F0.wireOp",EDGE,"E71.trimOffspring"),sQuery(id+"F0.wireOp",EDGE,"E72.trimOffspring"),sQuery(id+"F0.wireOp",EDGE,"E73.trimOffspring"),sQuery(id+"F0.wireOp",EDGE,"E74.trimOffspring"),sQuery(id+"F0.wireOp",EDGE,"E75.trimOffspring"),sQuery(id+"F0.wireOp",EDGE,"E76.trimOffspring"),sQuery(id+"F0.wireOp",EDGE,"E77.trimOffspring"),sQuery(id+"F0.wireOp",EDGE,"E78.trimOffspring"),sQuery(id+"F0.wireOp",EDGE,"E79.trimOffspring"),sQuery(id+"F0.wireOp",EDGE,"E80.trimOffspring"),sQuery(id+"F0.wireOp",EDGE,"E81.trimOffspring"),sQuery(id+"F0.wireOp",EDGE,"E82.trimOffspring"),sQuery(id+"F0.wireOp",EDGE,"E83.trimOffspring"),sQuery(id+"F0.wireOp",EDGE,"E84.trimOffspring"),sQuery(id+"F0.wireOp",EDGE,"E85.trimOffspring")])],"isStart":false});
            var sketch = newSketch(context, id + "F3", { "sketchPlane" : qUnion([Q0])});
            skCircle(sketch, "E86", {"center": v(0, 0) * mm, "radius": 6.35 * mm});
            skCircle(sketch, "E87", {"center": v(50.8, 0) * mm, "radius": 6.35 * mm});
            skCircle(sketch, "E88.1.0", {"center": v(-25.4, 44) * mm, "radius": 6.35 * mm});
            skCircle(sketch, "E88.2.0", {"center": v(-25.4, -44) * mm, "radius": 6.35 * mm});
            skSolve(sketch);
        }
        {
            var Q0;
            Q0=qSketchRegion(id+"F3",true);
            var Q1;
            Q1=makeQuery(id+"F3.imprint","IMPRINT",FACE,{"disambiguationData":[TD([[makeQuery(id+"F3.imprint","IMPRINT",EDGE,{"derivedFrom":sQuery(id+"F3.wireOp",EDGE,"E86")}),1.0]])]});
            extrude(context, id + "F4", {"entities" : qUnion([Q0, Q1]), "operationType" : NewBodyOperationType.ADD, "depth" : 6.35 * mm});
        }
    });
